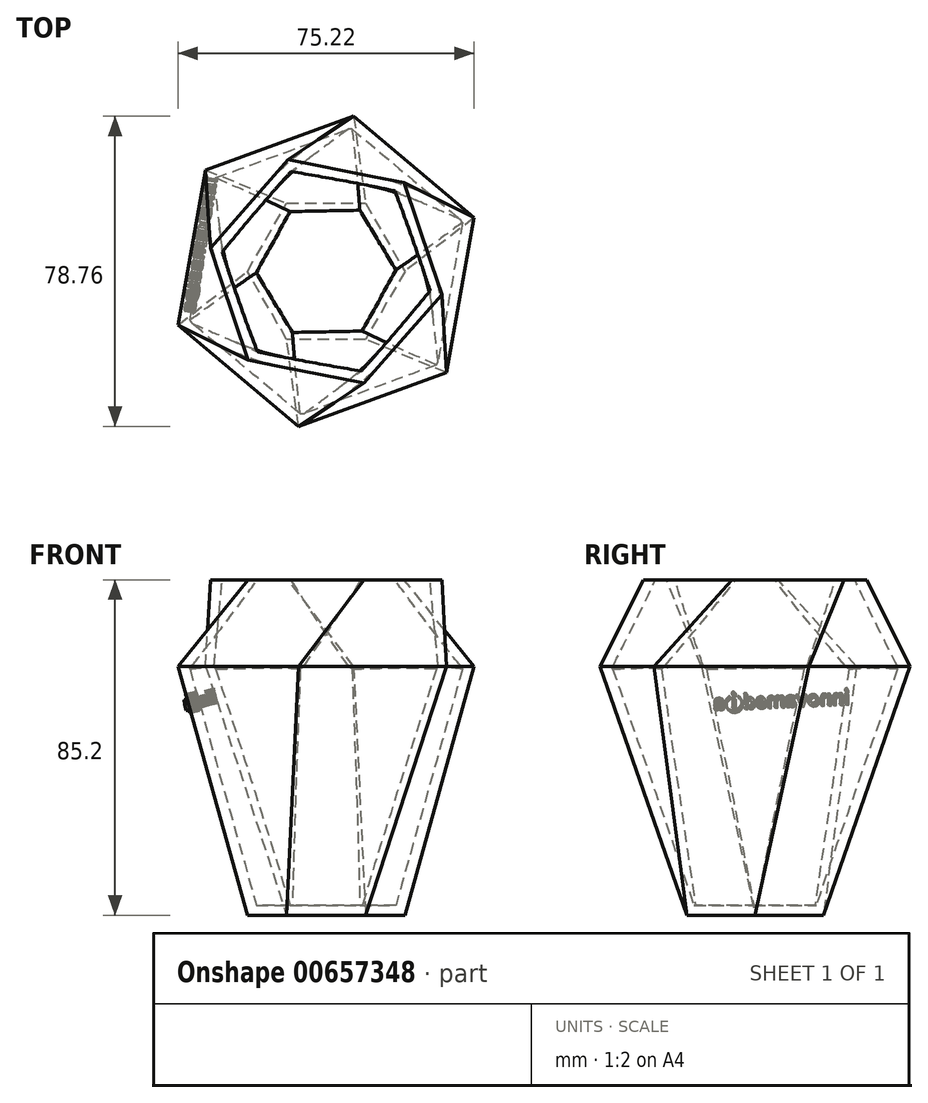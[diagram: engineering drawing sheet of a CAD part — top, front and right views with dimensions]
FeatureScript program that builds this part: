
annotation { "Feature Type Name" : "Feature", "Feature Type Description" : "" }
export const myFeature = defineFeature(function(context is Context, id is Id, definition is map)
    precondition{}
    {
        {
            var Q0;
            Q0=qCreatedBy(makeId("Top.planeOp"),FACE);
            var sketch = newSketch(context, id + "F0", { "sketchPlane" : qUnion([Q0])});
            skCircle(sketch, "E0.cCircle", {"center": v(0, 0) * mm, "radius": 17.32 * mm, "construction": true});
            skLineSegment(sketch, "E0.0", {"start": v(-10, 17.32) * mm, "end": v(10, 17.32) * mm});
            skLineSegment(sketch, "E0.1", {"start": v(10, 17.32) * mm, "end": v(20, 0) * mm});
            skLineSegment(sketch, "E0.2", {"start": v(20, 0) * mm, "end": v(10, -17.32) * mm});
            skLineSegment(sketch, "E0.3", {"start": v(10, -17.32) * mm, "end": v(-10, -17.32) * mm});
            skLineSegment(sketch, "E0.4", {"start": v(-10, -17.32) * mm, "end": v(-20, 0) * mm});
            skLineSegment(sketch, "E0.5", {"start": v(-20, 0) * mm, "end": v(-10, 17.32) * mm});
            skPoint(sketch, "E0.0.midPoint", {"position": v(0, 17.32) * mm});
            skSolve(sketch);
        }
        {
            var Q0;
            Q0=qCreatedBy(makeId("Top.planeOp"),FACE);
            cPlane(context, id + "F1", {"entities" : qUnion([Q0]), "cplaneType" : CPlaneType.OFFSET, "offset" : 63.2 * mm, "width" : 150 * mm, "height" : 150 * mm});
        }
        {
            var Q0;
            Q0=qCreatedBy(id+"F1.planeOp",FACE);
            var sketch = newSketch(context, id + "F2", { "sketchPlane" : qUnion([Q0])});
            skCircle(sketch, "E1.cCircle", {"center": v(0, 0) * mm, "radius": 34.64 * mm, "construction": true});
            skLineSegment(sketch, "E1.0", {"start": v(-30.6, 25.76) * mm, "end": v(7, 39.38) * mm});
            skLineSegment(sketch, "E1.1", {"start": v(7, 39.38) * mm, "end": v(37.6, 13.62) * mm});
            skLineSegment(sketch, "E1.2", {"start": v(37.6, 13.62) * mm, "end": v(30.6, -25.76) * mm});
            skLineSegment(sketch, "E1.3", {"start": v(30.6, -25.76) * mm, "end": v(-7, -39.38) * mm});
            skLineSegment(sketch, "E1.4", {"start": v(-7, -39.38) * mm, "end": v(-37.6, -13.62) * mm});
            skLineSegment(sketch, "E1.5", {"start": v(-37.6, -13.62) * mm, "end": v(-30.6, 25.76) * mm});
            skPoint(sketch, "E1.0.midPoint", {"position": v(-11.8, 32.57) * mm});
            skSolve(sketch);
        }
        {
            var Q0;
            Q0=makeQuery(id+"F2.imprint","IMPRINT",FACE,{"disambiguationData":[TD([[makeQuery(id+"F2.imprint","IMPRINT",EDGE,{"derivedFrom":sQuery(id+"F2.wireOp",EDGE,"E1.0")}),-1.0]])]});
            var Q1;
            Q1=makeQuery(id+"F0.imprint","IMPRINT",FACE,{"disambiguationData":[TD([[makeQuery(id+"F0.imprint","IMPRINT",EDGE,{"derivedFrom":sQuery(id+"F0.wireOp",EDGE,"E0.0")}),-1.0]])]});
            loft(context, id + "F3", {"sheetProfilesArray" : [{ "sheetProfileEntities" : qUnion([Q0]) }, { "sheetProfileEntities" : qUnion([Q1]) }]});
        }
        {
            var Q0;
            Q0=makeQuery(id+"F3.opLoft","CAP_FACE",FACE,{"disambiguationData":[OSD([makeQuery(id+"F2.imprint","IMPRINT",FACE,{"disambiguationData":[TD([[makeQuery(id+"F2.imprint","IMPRINT",EDGE,{"derivedFrom":sQuery(id+"F2.wireOp",EDGE,"E1.0")}),-1.0]])]})])],"isStart":true});
            cPlane(context, id + "F4", {"entities" : qUnion([Q0]), "cplaneType" : CPlaneType.OFFSET, "offset" : 22 * mm, "width" : 150 * mm, "height" : 150 * mm});
        }
        {
            var Q0;
            Q0=qCreatedBy(id+"F4.planeOp",FACE);
            var sketch = newSketch(context, id + "F5", { "sketchPlane" : qUnion([Q0])});
            skCircle(sketch, "E2.cCircle", {"center": v(0, 0) * mm, "radius": 25.98 * mm, "construction": true});
            skLineSegment(sketch, "E2.0", {"start": v(-19.81, -22.53) * mm, "end": v(-29.42, 5.9) * mm});
            skLineSegment(sketch, "E2.1", {"start": v(-29.42, 5.9) * mm, "end": v(-9.6, 28.42) * mm});
            skLineSegment(sketch, "E2.2", {"start": v(-9.6, 28.42) * mm, "end": v(19.81, 22.53) * mm});
            skLineSegment(sketch, "E2.3", {"start": v(19.81, 22.53) * mm, "end": v(29.42, -5.9) * mm});
            skLineSegment(sketch, "E2.4", {"start": v(29.42, -5.9) * mm, "end": v(9.6, -28.42) * mm});
            skLineSegment(sketch, "E2.5", {"start": v(9.6, -28.42) * mm, "end": v(-19.81, -22.53) * mm});
            skSolve(sketch);
        }
        {
            var Q1;
            Q1=makeQuery(id+"F3.opLoft","CAP_FACE",FACE,{"disambiguationData":[OSD([makeQuery(id+"F2.imprint","IMPRINT",FACE,{"disambiguationData":[TD([[makeQuery(id+"F2.imprint","IMPRINT",EDGE,{"derivedFrom":sQuery(id+"F2.wireOp",EDGE,"E1.0")}),-1.0]])]})])],"isStart":true});
            var Q2;
            Q2=makeQuery(id+"F5.imprint","IMPRINT",FACE,{"disambiguationData":[TD([[makeQuery(id+"F5.imprint","IMPRINT",EDGE,{"derivedFrom":sQuery(id+"F5.wireOp",EDGE,"E2.1")}),-1.0]])]});
            loft(context, id + "F6", {"operationType" : NewBodyOperationType.ADD, "sheetProfilesArray" : [{ "sheetProfileEntities" : qUnion([Q1]) }, { "sheetProfileEntities" : qUnion([Q2]) }]});
        }
        {
            var Q0;
            Q0=makeQuery(id+"F6.opLoft","CAP_FACE",FACE,{"disambiguationData":[OSD([makeQuery(id+"F5.imprint","IMPRINT",FACE,{"disambiguationData":[TD([[makeQuery(id+"F5.imprint","IMPRINT",EDGE,{"derivedFrom":sQuery(id+"F5.wireOp",EDGE,"E2.1")}),-1.0]])]})])],"isStart":true});
            shell(context, id + "F7", {"entities" : qUnion([Q0]), "thickness" : 2.5 * mm});
        }
        {
            var Q0;
            Q0=sQuery(id+"F2.wireOp",VERTEX,"E1.0.start");
            var Q1;
            Q1=sQuery(id+"F2.wireOp",VERTEX,"E1.5.start");
            var Q2;
            Q2=sQuery(id+"F0.wireOp",VERTEX,"E0.5.start");
            cPlane(context, id + "F8", {"entities" : qUnion([Q0, Q1, Q2]), "cplaneType" : CPlaneType.THREE_POINT, "offset" : 25 * mm, "width" : 150 * mm, "height" : 150 * mm});
        }
        {
            var Q0;
            Q0=qCreatedBy(id+"F8.planeOp",FACE);
            var sketch = newSketch(context, id + "F9", { "sketchPlane" : qUnion([Q0])});
            skLineSegment(sketch, "E3", {"start": v(-20.7, 62.44) * mm, "end": v(-20.69, 62.48) * mm});
            skLineSegment(sketch, "E4", {"start": v(-20.69, 62.48) * mm, "end": v(-20.63, 62.6) * mm});
            skLineSegment(sketch, "E5", {"start": v(-20.63, 62.6) * mm, "end": v(-20.53, 62.68) * mm});
            skLineSegment(sketch, "E6", {"start": v(-20.53, 62.68) * mm, "end": v(-20.42, 62.73) * mm});
            skLineSegment(sketch, "E7", {"start": v(-20.42, 62.73) * mm, "end": v(-20.28, 62.73) * mm});
            skLineSegment(sketch, "E8", {"start": v(-20.28, 62.73) * mm, "end": v(-20.17, 62.69) * mm});
            skLineSegment(sketch, "E9", {"start": v(-20.17, 62.69) * mm, "end": v(-20.08, 62.61) * mm});
            skLineSegment(sketch, "E10", {"start": v(-20.08, 62.61) * mm, "end": v(-20.02, 62.5) * mm});
            skLineSegment(sketch, "E11", {"start": v(-20.02, 62.5) * mm, "end": v(-20, 62.38) * mm});
            skLineSegment(sketch, "E12", {"start": v(-20, 62.38) * mm, "end": v(-20.02, 62.25) * mm});
            skLineSegment(sketch, "E13", {"start": v(-20.02, 62.25) * mm, "end": v(-20.08, 62.15) * mm});
            skLineSegment(sketch, "E14", {"start": v(-20.08, 62.15) * mm, "end": v(-20.17, 62.08) * mm});
            skLineSegment(sketch, "E15", {"start": v(-20.17, 62.08) * mm, "end": v(-20.29, 62.04) * mm});
            skLineSegment(sketch, "E16", {"start": v(-20.29, 62.04) * mm, "end": v(-20.42, 62.04) * mm});
            skLineSegment(sketch, "E17", {"start": v(-20.42, 62.04) * mm, "end": v(-20.53, 62.07) * mm});
            skLineSegment(sketch, "E18", {"start": v(-20.53, 62.07) * mm, "end": v(-20.62, 62.15) * mm});
            skLineSegment(sketch, "E19", {"start": v(-20.62, 62.15) * mm, "end": v(-20.68, 62.27) * mm});
            skLineSegment(sketch, "E20", {"start": v(-20.68, 62.27) * mm, "end": v(-20.7, 62.3) * mm});
            skLineSegment(sketch, "E21", {"start": v(-20.7, 62.3) * mm, "end": v(-20.7, 62.44) * mm});
            skLineSegment(sketch, "E22", {"start": v(-3.45, 61.2) * mm, "end": v(-3.29, 61.39) * mm});
            skLineSegment(sketch, "E23", {"start": v(-3.29, 61.39) * mm, "end": v(-3.1, 61.52) * mm});
            skLineSegment(sketch, "E24", {"start": v(-3.1, 61.52) * mm, "end": v(-2.89, 61.6) * mm});
            skLineSegment(sketch, "E25", {"start": v(-2.89, 61.6) * mm, "end": v(-2.65, 61.63) * mm});
            skLineSegment(sketch, "E26", {"start": v(-2.65, 61.63) * mm, "end": v(-2.4, 61.6) * mm});
            skLineSegment(sketch, "E27", {"start": v(-2.4, 61.6) * mm, "end": v(-2.2, 61.5) * mm});
            skLineSegment(sketch, "E28", {"start": v(-2.2, 61.5) * mm, "end": v(-2.02, 61.35) * mm});
            skLineSegment(sketch, "E29", {"start": v(-2.02, 61.35) * mm, "end": v(-1.86, 61.17) * mm});
            skLineSegment(sketch, "E30", {"start": v(-1.86, 61.17) * mm, "end": v(-1.7, 61.35) * mm});
            skLineSegment(sketch, "E31", {"start": v(-1.7, 61.35) * mm, "end": v(-1.5, 61.49) * mm});
            skLineSegment(sketch, "E32", {"start": v(-1.5, 61.49) * mm, "end": v(-1.3, 61.58) * mm});
            skLineSegment(sketch, "E33", {"start": v(-1.3, 61.58) * mm, "end": v(-1.06, 61.62) * mm});
            skLineSegment(sketch, "E34", {"start": v(-1.06, 61.62) * mm, "end": v(-0.84, 61.62) * mm});
            skLineSegment(sketch, "E35", {"start": v(-0.84, 61.62) * mm, "end": v(-0.64, 61.57) * mm});
            skLineSegment(sketch, "E36", {"start": v(-0.64, 61.57) * mm, "end": v(-0.45, 61.48) * mm});
            skLineSegment(sketch, "E37", {"start": v(-0.45, 61.48) * mm, "end": v(-0.28, 61.35) * mm});
            skLineSegment(sketch, "E38", {"start": v(-0.28, 61.35) * mm, "end": v(-0.1, 61.1) * mm});
            skLineSegment(sketch, "E39", {"start": v(-0.1, 61.1) * mm, "end": v(-0.04, 60.8) * mm});
            skLineSegment(sketch, "E40", {"start": v(-0.04, 60.8) * mm, "end": v(-0.04, 58.92) * mm});
            skLineSegment(sketch, "E41", {"start": v(-0.04, 58.92) * mm, "end": v(-0.05, 58.87) * mm});
            skLineSegment(sketch, "E42", {"start": v(-0.05, 58.87) * mm, "end": v(-0.1, 58.86) * mm});
            skLineSegment(sketch, "E43", {"start": v(-0.1, 58.86) * mm, "end": v(-0.59, 58.86) * mm});
            skLineSegment(sketch, "E44", {"start": v(-0.59, 58.86) * mm, "end": v(-0.64, 58.87) * mm});
            skLineSegment(sketch, "E45", {"start": v(-0.64, 58.87) * mm, "end": v(-0.65, 58.93) * mm});
            skLineSegment(sketch, "E46", {"start": v(-0.65, 58.93) * mm, "end": v(-0.65, 60.1) * mm});
            skLineSegment(sketch, "E47", {"start": v(-0.65, 60.1) * mm, "end": v(-0.69, 60.63) * mm});
            skLineSegment(sketch, "E48", {"start": v(-0.69, 60.63) * mm, "end": v(-0.76, 60.82) * mm});
            skLineSegment(sketch, "E49", {"start": v(-0.76, 60.82) * mm, "end": v(-0.87, 60.95) * mm});
            skLineSegment(sketch, "E50", {"start": v(-0.87, 60.95) * mm, "end": v(-1.02, 61.02) * mm});
            skLineSegment(sketch, "E51", {"start": v(-1.02, 61.02) * mm, "end": v(-1.23, 61.04) * mm});
            skLineSegment(sketch, "E52", {"start": v(-1.23, 61.04) * mm, "end": v(-1.4, 61) * mm});
            skLineSegment(sketch, "E53", {"start": v(-1.4, 61) * mm, "end": v(-1.56, 60.9) * mm});
            skLineSegment(sketch, "E54", {"start": v(-1.56, 60.9) * mm, "end": v(-1.67, 60.77) * mm});
            skLineSegment(sketch, "E55", {"start": v(-1.67, 60.77) * mm, "end": v(-1.73, 60.6) * mm});
            skLineSegment(sketch, "E56", {"start": v(-1.73, 60.6) * mm, "end": v(-1.75, 60.43) * mm});
            skLineSegment(sketch, "E57", {"start": v(-1.75, 60.43) * mm, "end": v(-1.74, 58.93) * mm});
            skLineSegment(sketch, "E58", {"start": v(-1.74, 58.93) * mm, "end": v(-1.76, 58.87) * mm});
            skLineSegment(sketch, "E59", {"start": v(-1.76, 58.87) * mm, "end": v(-1.82, 58.86) * mm});
            skLineSegment(sketch, "E60", {"start": v(-1.82, 58.86) * mm, "end": v(-2.3, 58.86) * mm});
            skLineSegment(sketch, "E61", {"start": v(-2.3, 58.86) * mm, "end": v(-2.36, 58.87) * mm});
            skLineSegment(sketch, "E62", {"start": v(-2.36, 58.87) * mm, "end": v(-2.38, 58.93) * mm});
            skLineSegment(sketch, "E63", {"start": v(-2.38, 58.93) * mm, "end": v(-2.38, 60.36) * mm});
            skLineSegment(sketch, "E64", {"start": v(-2.38, 60.36) * mm, "end": v(-2.4, 60.56) * mm});
            skLineSegment(sketch, "E65", {"start": v(-2.4, 60.56) * mm, "end": v(-2.45, 60.75) * mm});
            skLineSegment(sketch, "E66", {"start": v(-2.45, 60.75) * mm, "end": v(-2.63, 60.97) * mm});
            skLineSegment(sketch, "E67", {"start": v(-2.63, 60.97) * mm, "end": v(-2.76, 61.03) * mm});
            skLineSegment(sketch, "E68", {"start": v(-2.76, 61.03) * mm, "end": v(-2.9, 61.05) * mm});
            skLineSegment(sketch, "E69", {"start": v(-2.9, 61.05) * mm, "end": v(-3.06, 61.03) * mm});
            skLineSegment(sketch, "E70", {"start": v(-3.06, 61.03) * mm, "end": v(-3.2, 60.96) * mm});
            skLineSegment(sketch, "E71", {"start": v(-3.2, 60.96) * mm, "end": v(-3.4, 60.73) * mm});
            skLineSegment(sketch, "E72", {"start": v(-3.4, 60.73) * mm, "end": v(-3.46, 60.57) * mm});
            skLineSegment(sketch, "E73", {"start": v(-3.46, 60.57) * mm, "end": v(-3.47, 60.4) * mm});
            skLineSegment(sketch, "E74", {"start": v(-3.47, 60.4) * mm, "end": v(-3.47, 58.94) * mm});
            skLineSegment(sketch, "E75", {"start": v(-3.47, 58.94) * mm, "end": v(-3.49, 58.87) * mm});
            skLineSegment(sketch, "E76", {"start": v(-3.49, 58.87) * mm, "end": v(-3.55, 58.86) * mm});
            skLineSegment(sketch, "E77", {"start": v(-3.55, 58.86) * mm, "end": v(-4.04, 58.86) * mm});
            skLineSegment(sketch, "E78", {"start": v(-4.04, 58.86) * mm, "end": v(-4.1, 58.87) * mm});
            skLineSegment(sketch, "E79", {"start": v(-4.1, 58.87) * mm, "end": v(-4.1, 58.92) * mm});
            skLineSegment(sketch, "E80", {"start": v(-4.1, 58.92) * mm, "end": v(-4.1, 61.5) * mm});
            skLineSegment(sketch, "E81", {"start": v(-4.1, 61.5) * mm, "end": v(-4.1, 61.55) * mm});
            skLineSegment(sketch, "E82", {"start": v(-4.1, 61.55) * mm, "end": v(-4.05, 61.57) * mm});
            skLineSegment(sketch, "E83", {"start": v(-4.05, 61.57) * mm, "end": v(-3.53, 61.57) * mm});
            skLineSegment(sketch, "E84", {"start": v(-3.53, 61.57) * mm, "end": v(-3.48, 61.56) * mm});
            skLineSegment(sketch, "E85", {"start": v(-3.48, 61.56) * mm, "end": v(-3.47, 61.5) * mm});
            skLineSegment(sketch, "E86", {"start": v(-3.47, 61.5) * mm, "end": v(-3.47, 61.22) * mm});
            skLineSegment(sketch, "E87", {"start": v(-3.47, 61.22) * mm, "end": v(-3.45, 61.2) * mm});
            skLineSegment(sketch, "E88", {"start": v(5.32, 61.2) * mm, "end": v(5.32, 62.22) * mm});
            skLineSegment(sketch, "E89", {"start": v(5.32, 62.22) * mm, "end": v(5.32, 62.48) * mm});
            skLineSegment(sketch, "E90", {"start": v(5.32, 62.48) * mm, "end": v(5.33, 62.53) * mm});
            skLineSegment(sketch, "E91", {"start": v(5.33, 62.53) * mm, "end": v(5.38, 62.54) * mm});
            skLineSegment(sketch, "E92", {"start": v(5.38, 62.54) * mm, "end": v(5.98, 62.54) * mm});
            skLineSegment(sketch, "E93", {"start": v(5.98, 62.54) * mm, "end": v(6.03, 62.52) * mm});
            skLineSegment(sketch, "E94", {"start": v(6.03, 62.52) * mm, "end": v(6.04, 62.47) * mm});
            skLineSegment(sketch, "E95", {"start": v(6.04, 62.47) * mm, "end": v(6.04, 61.51) * mm});
            skLineSegment(sketch, "E96", {"start": v(6.04, 61.51) * mm, "end": v(6.04, 58.9) * mm});
            skLineSegment(sketch, "E97", {"start": v(6.04, 58.9) * mm, "end": v(6.03, 58.82) * mm});
            skLineSegment(sketch, "E98", {"start": v(6.03, 58.82) * mm, "end": v(5.94, 58.8) * mm});
            skLineSegment(sketch, "E99", {"start": v(5.94, 58.8) * mm, "end": v(5.43, 58.8) * mm});
            skLineSegment(sketch, "E100", {"start": v(5.43, 58.8) * mm, "end": v(5.38, 58.82) * mm});
            skLineSegment(sketch, "E101", {"start": v(5.38, 58.82) * mm, "end": v(5.37, 58.87) * mm});
            skLineSegment(sketch, "E102", {"start": v(5.37, 58.87) * mm, "end": v(5.37, 59.17) * mm});
            skLineSegment(sketch, "E103", {"start": v(5.37, 59.17) * mm, "end": v(5.33, 59.14) * mm});
            skLineSegment(sketch, "E104", {"start": v(5.33, 59.14) * mm, "end": v(5.13, 58.95) * mm});
            skLineSegment(sketch, "E105", {"start": v(5.13, 58.95) * mm, "end": v(4.9, 58.82) * mm});
            skLineSegment(sketch, "E106", {"start": v(4.9, 58.82) * mm, "end": v(4.67, 58.75) * mm});
            skLineSegment(sketch, "E107", {"start": v(4.67, 58.75) * mm, "end": v(4.43, 58.74) * mm});
            skLineSegment(sketch, "E108", {"start": v(4.43, 58.74) * mm, "end": v(4.2, 58.8) * mm});
            skLineSegment(sketch, "E109", {"start": v(4.2, 58.8) * mm, "end": v(3.97, 58.9) * mm});
            skLineSegment(sketch, "E110", {"start": v(3.97, 58.9) * mm, "end": v(3.77, 59.07) * mm});
            skLineSegment(sketch, "E111", {"start": v(3.77, 59.07) * mm, "end": v(3.6, 59.29) * mm});
            skLineSegment(sketch, "E112", {"start": v(3.6, 59.29) * mm, "end": v(3.46, 59.62) * mm});
            skLineSegment(sketch, "E113", {"start": v(3.46, 59.62) * mm, "end": v(3.4, 59.97) * mm});
            skLineSegment(sketch, "E114", {"start": v(3.4, 59.97) * mm, "end": v(3.4, 60.4) * mm});
            skLineSegment(sketch, "E115", {"start": v(3.4, 60.4) * mm, "end": v(3.49, 60.8) * mm});
            skLineSegment(sketch, "E116", {"start": v(3.49, 60.8) * mm, "end": v(3.59, 61.03) * mm});
            skLineSegment(sketch, "E117", {"start": v(3.59, 61.03) * mm, "end": v(3.72, 61.21) * mm});
            skLineSegment(sketch, "E118", {"start": v(3.72, 61.21) * mm, "end": v(3.88, 61.36) * mm});
            skLineSegment(sketch, "E119", {"start": v(3.88, 61.36) * mm, "end": v(4.07, 61.47) * mm});
            skLineSegment(sketch, "E120", {"start": v(4.07, 61.47) * mm, "end": v(4.47, 61.57) * mm});
            skLineSegment(sketch, "E121", {"start": v(4.47, 61.57) * mm, "end": v(4.88, 61.5) * mm});
            skLineSegment(sketch, "E122", {"start": v(4.88, 61.5) * mm, "end": v(5.11, 61.39) * mm});
            skLineSegment(sketch, "E123", {"start": v(5.11, 61.39) * mm, "end": v(5.32, 61.2) * mm});
            skLineSegment(sketch, "E124", {"start": v(5.32, 60.15) * mm, "end": v(5.3, 60.4) * mm});
            skLineSegment(sketch, "E125", {"start": v(5.3, 60.4) * mm, "end": v(5.25, 60.64) * mm});
            skLineSegment(sketch, "E126", {"start": v(5.25, 60.64) * mm, "end": v(5.14, 60.83) * mm});
            skLineSegment(sketch, "E127", {"start": v(5.14, 60.83) * mm, "end": v(4.97, 60.96) * mm});
            skLineSegment(sketch, "E128", {"start": v(4.97, 60.96) * mm, "end": v(4.78, 61.02) * mm});
            skLineSegment(sketch, "E129", {"start": v(4.78, 61.02) * mm, "end": v(4.57, 61) * mm});
            skLineSegment(sketch, "E130", {"start": v(4.57, 61) * mm, "end": v(4.42, 60.93) * mm});
            skLineSegment(sketch, "E131", {"start": v(4.42, 60.93) * mm, "end": v(4.31, 60.83) * mm});
            skLineSegment(sketch, "E132", {"start": v(4.31, 60.83) * mm, "end": v(4.18, 60.56) * mm});
            skLineSegment(sketch, "E133", {"start": v(4.18, 60.56) * mm, "end": v(4.13, 60.14) * mm});
            skLineSegment(sketch, "E134", {"start": v(4.13, 60.14) * mm, "end": v(4.2, 59.73) * mm});
            skLineSegment(sketch, "E135", {"start": v(4.2, 59.73) * mm, "end": v(4.3, 59.52) * mm});
            skLineSegment(sketch, "E136", {"start": v(4.3, 59.52) * mm, "end": v(4.47, 59.37) * mm});
            skLineSegment(sketch, "E137", {"start": v(4.47, 59.37) * mm, "end": v(4.68, 59.3) * mm});
            skLineSegment(sketch, "E138", {"start": v(4.68, 59.3) * mm, "end": v(4.89, 59.33) * mm});
            skLineSegment(sketch, "E139", {"start": v(4.89, 59.33) * mm, "end": v(5.07, 59.44) * mm});
            skLineSegment(sketch, "E140", {"start": v(5.07, 59.44) * mm, "end": v(5.22, 59.62) * mm});
            skLineSegment(sketch, "E141", {"start": v(5.22, 59.62) * mm, "end": v(5.3, 59.88) * mm});
            skLineSegment(sketch, "E142", {"start": v(5.3, 59.88) * mm, "end": v(5.32, 60.15) * mm});
            skLineSegment(sketch, "E143", {"start": v(2.08, 59.95) * mm, "end": v(1.26, 59.95) * mm});
            skLineSegment(sketch, "E144", {"start": v(1.26, 59.95) * mm, "end": v(1.2, 59.93) * mm});
            skLineSegment(sketch, "E145", {"start": v(1.2, 59.93) * mm, "end": v(1.2, 59.88) * mm});
            skLineSegment(sketch, "E146", {"start": v(1.2, 59.88) * mm, "end": v(1.27, 59.6) * mm});
            skLineSegment(sketch, "E147", {"start": v(1.27, 59.6) * mm, "end": v(1.44, 59.4) * mm});
            skLineSegment(sketch, "E148", {"start": v(1.44, 59.4) * mm, "end": v(1.67, 59.29) * mm});
            skLineSegment(sketch, "E149", {"start": v(1.67, 59.29) * mm, "end": v(1.93, 59.3) * mm});
            skLineSegment(sketch, "E150", {"start": v(1.93, 59.3) * mm, "end": v(2.1, 59.42) * mm});
            skLineSegment(sketch, "E151", {"start": v(2.1, 59.42) * mm, "end": v(2.2, 59.6) * mm});
            skLineSegment(sketch, "E152", {"start": v(2.2, 59.6) * mm, "end": v(2.24, 59.65) * mm});
            skLineSegment(sketch, "E153", {"start": v(2.24, 59.65) * mm, "end": v(2.3, 59.66) * mm});
            skLineSegment(sketch, "E154", {"start": v(2.3, 59.66) * mm, "end": v(2.87, 59.56) * mm});
            skLineSegment(sketch, "E155", {"start": v(2.87, 59.56) * mm, "end": v(2.93, 59.54) * mm});
            skLineSegment(sketch, "E156", {"start": v(2.93, 59.54) * mm, "end": v(2.92, 59.47) * mm});
            skLineSegment(sketch, "E157", {"start": v(2.92, 59.47) * mm, "end": v(2.74, 59.17) * mm});
            skLineSegment(sketch, "E158", {"start": v(2.74, 59.17) * mm, "end": v(2.5, 58.94) * mm});
            skLineSegment(sketch, "E159", {"start": v(2.5, 58.94) * mm, "end": v(2.22, 58.8) * mm});
            skLineSegment(sketch, "E160", {"start": v(2.22, 58.8) * mm, "end": v(1.87, 58.74) * mm});
            skLineSegment(sketch, "E161", {"start": v(1.87, 58.74) * mm, "end": v(1.6, 58.74) * mm});
            skLineSegment(sketch, "E162", {"start": v(1.6, 58.74) * mm, "end": v(1.34, 58.79) * mm});
            skLineSegment(sketch, "E163", {"start": v(1.34, 58.79) * mm, "end": v(1.1, 58.88) * mm});
            skLineSegment(sketch, "E164", {"start": v(1.1, 58.88) * mm, "end": v(0.9, 59) * mm});
            skLineSegment(sketch, "E165", {"start": v(0.9, 59) * mm, "end": v(0.74, 59.18) * mm});
            skLineSegment(sketch, "E166", {"start": v(0.74, 59.18) * mm, "end": v(0.6, 59.4) * mm});
            skLineSegment(sketch, "E167", {"start": v(0.6, 59.4) * mm, "end": v(0.49, 59.77) * mm});
            skLineSegment(sketch, "E168", {"start": v(0.49, 59.77) * mm, "end": v(0.45, 60.14) * mm});
            skLineSegment(sketch, "E169", {"start": v(0.45, 60.14) * mm, "end": v(0.49, 60.52) * mm});
            skLineSegment(sketch, "E170", {"start": v(0.49, 60.52) * mm, "end": v(0.61, 60.89) * mm});
            skLineSegment(sketch, "E171", {"start": v(0.61, 60.89) * mm, "end": v(0.82, 61.2) * mm});
            skLineSegment(sketch, "E172", {"start": v(0.82, 61.2) * mm, "end": v(1.12, 61.43) * mm});
            skLineSegment(sketch, "E173", {"start": v(1.12, 61.43) * mm, "end": v(1.48, 61.55) * mm});
            skLineSegment(sketch, "E174", {"start": v(1.48, 61.55) * mm, "end": v(1.87, 61.56) * mm});
            skLineSegment(sketch, "E175", {"start": v(1.87, 61.56) * mm, "end": v(2.15, 61.5) * mm});
            skLineSegment(sketch, "E176", {"start": v(2.15, 61.5) * mm, "end": v(2.4, 61.39) * mm});
            skLineSegment(sketch, "E177", {"start": v(2.4, 61.39) * mm, "end": v(2.6, 61.22) * mm});
            skLineSegment(sketch, "E178", {"start": v(2.6, 61.22) * mm, "end": v(2.77, 61) * mm});
            skLineSegment(sketch, "E179", {"start": v(2.77, 61) * mm, "end": v(2.89, 60.72) * mm});
            skLineSegment(sketch, "E180", {"start": v(2.89, 60.72) * mm, "end": v(2.95, 60.42) * mm});
            skLineSegment(sketch, "E181", {"start": v(2.95, 60.42) * mm, "end": v(2.98, 60.02) * mm});
            skLineSegment(sketch, "E182", {"start": v(2.98, 60.02) * mm, "end": v(2.97, 59.96) * mm});
            skLineSegment(sketch, "E183", {"start": v(2.97, 59.96) * mm, "end": v(2.91, 59.95) * mm});
            skLineSegment(sketch, "E184", {"start": v(2.91, 59.95) * mm, "end": v(2.08, 59.95) * mm});
            skLineSegment(sketch, "E185", {"start": v(1.74, 60.39) * mm, "end": v(2.11, 60.39) * mm});
            skLineSegment(sketch, "E186", {"start": v(2.11, 60.39) * mm, "end": v(2.25, 60.4) * mm});
            skLineSegment(sketch, "E187", {"start": v(2.25, 60.4) * mm, "end": v(2.25, 60.55) * mm});
            skLineSegment(sketch, "E188", {"start": v(2.25, 60.55) * mm, "end": v(2.17, 60.78) * mm});
            skLineSegment(sketch, "E189", {"start": v(2.17, 60.78) * mm, "end": v(2.01, 60.94) * mm});
            skLineSegment(sketch, "E190", {"start": v(2.01, 60.94) * mm, "end": v(1.81, 61.01) * mm});
            skLineSegment(sketch, "E191", {"start": v(1.81, 61.01) * mm, "end": v(1.58, 61) * mm});
            skLineSegment(sketch, "E192", {"start": v(1.58, 61) * mm, "end": v(1.43, 60.92) * mm});
            skLineSegment(sketch, "E193", {"start": v(1.43, 60.92) * mm, "end": v(1.32, 60.8) * mm});
            skLineSegment(sketch, "E194", {"start": v(1.32, 60.8) * mm, "end": v(1.24, 60.64) * mm});
            skLineSegment(sketch, "E195", {"start": v(1.24, 60.64) * mm, "end": v(1.2, 60.45) * mm});
            skLineSegment(sketch, "E196", {"start": v(1.2, 60.45) * mm, "end": v(1.22, 60.4) * mm});
            skLineSegment(sketch, "E197", {"start": v(1.22, 60.4) * mm, "end": v(1.27, 60.39) * mm});
            skLineSegment(sketch, "E198", {"start": v(1.27, 60.39) * mm, "end": v(1.74, 60.39) * mm});
            skLineSegment(sketch, "E199", {"start": v(-5.33, 59.15) * mm, "end": v(-5.5, 59.02) * mm});
            skLineSegment(sketch, "E200", {"start": v(-5.5, 59.02) * mm, "end": v(-5.77, 58.87) * mm});
            skLineSegment(sketch, "E201", {"start": v(-5.77, 58.87) * mm, "end": v(-6.07, 58.8) * mm});
            skLineSegment(sketch, "E202", {"start": v(-6.07, 58.8) * mm, "end": v(-6.36, 58.8) * mm});
            skLineSegment(sketch, "E203", {"start": v(-6.36, 58.8) * mm, "end": v(-6.67, 58.9) * mm});
            skLineSegment(sketch, "E204", {"start": v(-6.67, 58.9) * mm, "end": v(-6.89, 59.05) * mm});
            skLineSegment(sketch, "E205", {"start": v(-6.89, 59.05) * mm, "end": v(-7.04, 59.23) * mm});
            skLineSegment(sketch, "E206", {"start": v(-7.04, 59.23) * mm, "end": v(-7.13, 59.46) * mm});
            skLineSegment(sketch, "E207", {"start": v(-7.13, 59.46) * mm, "end": v(-7.14, 59.72) * mm});
            skLineSegment(sketch, "E208", {"start": v(-7.14, 59.72) * mm, "end": v(-7.1, 59.97) * mm});
            skLineSegment(sketch, "E209", {"start": v(-7.1, 59.97) * mm, "end": v(-6.98, 60.17) * mm});
            skLineSegment(sketch, "E210", {"start": v(-6.98, 60.17) * mm, "end": v(-6.81, 60.33) * mm});
            skLineSegment(sketch, "E211", {"start": v(-6.81, 60.33) * mm, "end": v(-6.58, 60.45) * mm});
            skLineSegment(sketch, "E212", {"start": v(-6.58, 60.45) * mm, "end": v(-6.28, 60.52) * mm});
            skLineSegment(sketch, "E213", {"start": v(-6.28, 60.52) * mm, "end": v(-5.98, 60.54) * mm});
            skLineSegment(sketch, "E214", {"start": v(-5.98, 60.54) * mm, "end": v(-5.68, 60.52) * mm});
            skLineSegment(sketch, "E215", {"start": v(-5.68, 60.52) * mm, "end": v(-5.38, 60.45) * mm});
            skLineSegment(sketch, "E216", {"start": v(-5.38, 60.45) * mm, "end": v(-5.33, 60.43) * mm});
            skLineSegment(sketch, "E217", {"start": v(-5.33, 60.43) * mm, "end": v(-5.32, 60.43) * mm});
            skLineSegment(sketch, "E218", {"start": v(-5.32, 60.43) * mm, "end": v(-5.33, 60.64) * mm});
            skLineSegment(sketch, "E219", {"start": v(-5.33, 60.64) * mm, "end": v(-5.42, 60.82) * mm});
            skLineSegment(sketch, "E220", {"start": v(-5.42, 60.82) * mm, "end": v(-5.58, 60.95) * mm});
            skLineSegment(sketch, "E221", {"start": v(-5.58, 60.95) * mm, "end": v(-5.79, 61.03) * mm});
            skLineSegment(sketch, "E222", {"start": v(-5.79, 61.03) * mm, "end": v(-6.24, 61.03) * mm});
            skLineSegment(sketch, "E223", {"start": v(-6.24, 61.03) * mm, "end": v(-6.67, 60.9) * mm});
            skLineSegment(sketch, "E224", {"start": v(-6.67, 60.9) * mm, "end": v(-6.73, 60.9) * mm});
            skLineSegment(sketch, "E225", {"start": v(-6.73, 60.9) * mm, "end": v(-6.77, 60.94) * mm});
            skLineSegment(sketch, "E226", {"start": v(-6.77, 60.94) * mm, "end": v(-6.9, 61.34) * mm});
            skLineSegment(sketch, "E227", {"start": v(-6.9, 61.34) * mm, "end": v(-6.9, 61.38) * mm});
            skLineSegment(sketch, "E228", {"start": v(-6.9, 61.38) * mm, "end": v(-6.86, 61.4) * mm});
            skLineSegment(sketch, "E229", {"start": v(-6.86, 61.4) * mm, "end": v(-6.44, 61.55) * mm});
            skLineSegment(sketch, "E230", {"start": v(-6.44, 61.55) * mm, "end": v(-6, 61.6) * mm});
            skLineSegment(sketch, "E231", {"start": v(-6, 61.6) * mm, "end": v(-5.66, 61.6) * mm});
            skLineSegment(sketch, "E232", {"start": v(-5.66, 61.6) * mm, "end": v(-5.33, 61.5) * mm});
            skLineSegment(sketch, "E233", {"start": v(-5.33, 61.5) * mm, "end": v(-5.08, 61.37) * mm});
            skLineSegment(sketch, "E234", {"start": v(-5.08, 61.37) * mm, "end": v(-4.9, 61.18) * mm});
            skLineSegment(sketch, "E235", {"start": v(-4.9, 61.18) * mm, "end": v(-4.77, 60.95) * mm});
            skLineSegment(sketch, "E236", {"start": v(-4.77, 60.95) * mm, "end": v(-4.72, 60.67) * mm});
            skLineSegment(sketch, "E237", {"start": v(-4.72, 60.67) * mm, "end": v(-4.7, 59.49) * mm});
            skLineSegment(sketch, "E238", {"start": v(-4.7, 59.49) * mm, "end": v(-4.7, 58.93) * mm});
            skLineSegment(sketch, "E239", {"start": v(-4.7, 58.93) * mm, "end": v(-4.72, 58.88) * mm});
            skLineSegment(sketch, "E240", {"start": v(-4.72, 58.88) * mm, "end": v(-4.77, 58.86) * mm});
            skLineSegment(sketch, "E241", {"start": v(-4.77, 58.86) * mm, "end": v(-5.28, 58.86) * mm});
            skLineSegment(sketch, "E242", {"start": v(-5.28, 58.86) * mm, "end": v(-5.32, 58.88) * mm});
            skLineSegment(sketch, "E243", {"start": v(-5.32, 58.88) * mm, "end": v(-5.34, 58.92) * mm});
            skLineSegment(sketch, "E244", {"start": v(-5.34, 58.92) * mm, "end": v(-5.33, 59.15) * mm});
            skLineSegment(sketch, "E245", {"start": v(-5.98, 59.28) * mm, "end": v(-5.9, 59.28) * mm});
            skLineSegment(sketch, "E246", {"start": v(-5.9, 59.28) * mm, "end": v(-5.65, 59.34) * mm});
            skLineSegment(sketch, "E247", {"start": v(-5.65, 59.34) * mm, "end": v(-5.46, 59.48) * mm});
            skLineSegment(sketch, "E248", {"start": v(-5.46, 59.48) * mm, "end": v(-5.35, 59.67) * mm});
            skLineSegment(sketch, "E249", {"start": v(-5.35, 59.67) * mm, "end": v(-5.31, 59.9) * mm});
            skLineSegment(sketch, "E250", {"start": v(-5.31, 59.9) * mm, "end": v(-5.33, 59.99) * mm});
            skLineSegment(sketch, "E251", {"start": v(-5.33, 59.99) * mm, "end": v(-5.4, 60.03) * mm});
            skLineSegment(sketch, "E252", {"start": v(-5.4, 60.03) * mm, "end": v(-5.92, 60.1) * mm});
            skLineSegment(sketch, "E253", {"start": v(-5.92, 60.1) * mm, "end": v(-6.17, 60.06) * mm});
            skLineSegment(sketch, "E254", {"start": v(-6.17, 60.06) * mm, "end": v(-6.39, 59.95) * mm});
            skLineSegment(sketch, "E255", {"start": v(-6.39, 59.95) * mm, "end": v(-6.49, 59.83) * mm});
            skLineSegment(sketch, "E256", {"start": v(-6.49, 59.83) * mm, "end": v(-6.53, 59.7) * mm});
            skLineSegment(sketch, "E257", {"start": v(-6.53, 59.7) * mm, "end": v(-6.5, 59.55) * mm});
            skLineSegment(sketch, "E258", {"start": v(-6.5, 59.55) * mm, "end": v(-6.4, 59.42) * mm});
            skLineSegment(sketch, "E259", {"start": v(-6.4, 59.42) * mm, "end": v(-6.22, 59.3) * mm});
            skLineSegment(sketch, "E260", {"start": v(-6.22, 59.3) * mm, "end": v(-5.98, 59.28) * mm});
            skLineSegment(sketch, "E261", {"start": v(13.1, 59.14) * mm, "end": v(12.96, 59.04) * mm});
            skLineSegment(sketch, "E262", {"start": v(12.96, 59.04) * mm, "end": v(12.65, 58.87) * mm});
            skLineSegment(sketch, "E263", {"start": v(12.65, 58.87) * mm, "end": v(12.31, 58.8) * mm});
            skLineSegment(sketch, "E264", {"start": v(12.31, 58.8) * mm, "end": v(11.97, 58.83) * mm});
            skLineSegment(sketch, "E265", {"start": v(11.97, 58.83) * mm, "end": v(11.66, 58.96) * mm});
            skLineSegment(sketch, "E266", {"start": v(11.66, 58.96) * mm, "end": v(11.49, 59.1) * mm});
            skLineSegment(sketch, "E267", {"start": v(11.49, 59.1) * mm, "end": v(11.36, 59.27) * mm});
            skLineSegment(sketch, "E268", {"start": v(11.36, 59.27) * mm, "end": v(11.3, 59.47) * mm});
            skLineSegment(sketch, "E269", {"start": v(11.3, 59.47) * mm, "end": v(11.28, 59.7) * mm});
            skLineSegment(sketch, "E270", {"start": v(11.28, 59.7) * mm, "end": v(11.32, 59.94) * mm});
            skLineSegment(sketch, "E271", {"start": v(11.32, 59.94) * mm, "end": v(11.42, 60.14) * mm});
            skLineSegment(sketch, "E272", {"start": v(11.42, 60.14) * mm, "end": v(11.58, 60.3) * mm});
            skLineSegment(sketch, "E273", {"start": v(11.58, 60.3) * mm, "end": v(11.8, 60.43) * mm});
            skLineSegment(sketch, "E274", {"start": v(11.8, 60.43) * mm, "end": v(12.15, 60.53) * mm});
            skLineSegment(sketch, "E275", {"start": v(12.15, 60.53) * mm, "end": v(12.53, 60.54) * mm});
            skLineSegment(sketch, "E276", {"start": v(12.53, 60.54) * mm, "end": v(12.82, 60.51) * mm});
            skLineSegment(sketch, "E277", {"start": v(12.82, 60.51) * mm, "end": v(13.1, 60.43) * mm});
            skLineSegment(sketch, "E278", {"start": v(13.1, 60.43) * mm, "end": v(13.1, 60.6) * mm});
            skLineSegment(sketch, "E279", {"start": v(13.1, 60.6) * mm, "end": v(13.04, 60.76) * mm});
            skLineSegment(sketch, "E280", {"start": v(13.04, 60.76) * mm, "end": v(12.93, 60.9) * mm});
            skLineSegment(sketch, "E281", {"start": v(12.93, 60.9) * mm, "end": v(12.77, 60.98) * mm});
            skLineSegment(sketch, "E282", {"start": v(12.77, 60.98) * mm, "end": v(12.44, 61.04) * mm});
            skLineSegment(sketch, "E283", {"start": v(12.44, 61.04) * mm, "end": v(12.1, 61) * mm});
            skLineSegment(sketch, "E284", {"start": v(12.1, 61) * mm, "end": v(11.75, 60.9) * mm});
            skLineSegment(sketch, "E285", {"start": v(11.75, 60.9) * mm, "end": v(11.7, 60.89) * mm});
            skLineSegment(sketch, "E286", {"start": v(11.7, 60.89) * mm, "end": v(11.66, 60.94) * mm});
            skLineSegment(sketch, "E287", {"start": v(11.66, 60.94) * mm, "end": v(11.53, 61.34) * mm});
            skLineSegment(sketch, "E288", {"start": v(11.53, 61.34) * mm, "end": v(11.53, 61.38) * mm});
            skLineSegment(sketch, "E289", {"start": v(11.53, 61.38) * mm, "end": v(11.57, 61.4) * mm});
            skLineSegment(sketch, "E290", {"start": v(11.57, 61.4) * mm, "end": v(11.89, 61.52) * mm});
            skLineSegment(sketch, "E291", {"start": v(11.89, 61.52) * mm, "end": v(12.22, 61.6) * mm});
            skLineSegment(sketch, "E292", {"start": v(12.22, 61.6) * mm, "end": v(12.62, 61.61) * mm});
            skLineSegment(sketch, "E293", {"start": v(12.62, 61.61) * mm, "end": v(13.02, 61.54) * mm});
            skLineSegment(sketch, "E294", {"start": v(13.02, 61.54) * mm, "end": v(13.31, 61.4) * mm});
            skLineSegment(sketch, "E295", {"start": v(13.31, 61.4) * mm, "end": v(13.53, 61.2) * mm});
            skLineSegment(sketch, "E296", {"start": v(13.53, 61.2) * mm, "end": v(13.67, 60.92) * mm});
            skLineSegment(sketch, "E297", {"start": v(13.67, 60.92) * mm, "end": v(13.72, 60.6) * mm});
            skLineSegment(sketch, "E298", {"start": v(13.72, 60.6) * mm, "end": v(13.72, 58.92) * mm});
            skLineSegment(sketch, "E299", {"start": v(13.72, 58.92) * mm, "end": v(13.71, 58.87) * mm});
            skLineSegment(sketch, "E300", {"start": v(13.71, 58.87) * mm, "end": v(13.66, 58.86) * mm});
            skLineSegment(sketch, "E301", {"start": v(13.66, 58.86) * mm, "end": v(13.15, 58.86) * mm});
            skLineSegment(sketch, "E302", {"start": v(13.15, 58.86) * mm, "end": v(13.1, 58.87) * mm});
            skLineSegment(sketch, "E303", {"start": v(13.1, 58.87) * mm, "end": v(13.1, 58.93) * mm});
            skLineSegment(sketch, "E304", {"start": v(13.1, 58.93) * mm, "end": v(13.1, 59.14) * mm});
            skLineSegment(sketch, "E305", {"start": v(12.43, 59.28) * mm, "end": v(12.62, 59.3) * mm});
            skLineSegment(sketch, "E306", {"start": v(12.62, 59.3) * mm, "end": v(12.83, 59.38) * mm});
            skLineSegment(sketch, "E307", {"start": v(12.83, 59.38) * mm, "end": v(13, 59.5) * mm});
            skLineSegment(sketch, "E308", {"start": v(13, 59.5) * mm, "end": v(13.09, 59.68) * mm});
            skLineSegment(sketch, "E309", {"start": v(13.09, 59.68) * mm, "end": v(13.11, 59.9) * mm});
            skLineSegment(sketch, "E310", {"start": v(13.11, 59.9) * mm, "end": v(13.09, 59.98) * mm});
            skLineSegment(sketch, "E311", {"start": v(13.09, 59.98) * mm, "end": v(13.01, 60.03) * mm});
            skLineSegment(sketch, "E312", {"start": v(13.01, 60.03) * mm, "end": v(12.58, 60.09) * mm});
            skLineSegment(sketch, "E313", {"start": v(12.58, 60.09) * mm, "end": v(12.31, 60.07) * mm});
            skLineSegment(sketch, "E314", {"start": v(12.31, 60.07) * mm, "end": v(12.07, 59.97) * mm});
            skLineSegment(sketch, "E315", {"start": v(12.07, 59.97) * mm, "end": v(11.95, 59.84) * mm});
            skLineSegment(sketch, "E316", {"start": v(11.95, 59.84) * mm, "end": v(11.9, 59.68) * mm});
            skLineSegment(sketch, "E317", {"start": v(11.9, 59.68) * mm, "end": v(11.94, 59.52) * mm});
            skLineSegment(sketch, "E318", {"start": v(11.94, 59.52) * mm, "end": v(12.06, 59.39) * mm});
            skLineSegment(sketch, "E319", {"start": v(12.06, 59.39) * mm, "end": v(12.24, 59.3) * mm});
            skLineSegment(sketch, "E320", {"start": v(12.24, 59.3) * mm, "end": v(12.43, 59.28) * mm});
            skLineSegment(sketch, "E321", {"start": v(-13.15, 60.22) * mm, "end": v(-13.12, 60.5) * mm});
            skLineSegment(sketch, "E322", {"start": v(-13.12, 60.5) * mm, "end": v(-13.04, 60.76) * mm});
            skLineSegment(sketch, "E323", {"start": v(-13.04, 60.76) * mm, "end": v(-12.91, 61) * mm});
            skLineSegment(sketch, "E324", {"start": v(-12.91, 61) * mm, "end": v(-12.74, 61.2) * mm});
            skLineSegment(sketch, "E325", {"start": v(-12.74, 61.2) * mm, "end": v(-12.53, 61.38) * mm});
            skLineSegment(sketch, "E326", {"start": v(-12.53, 61.38) * mm, "end": v(-12.29, 61.5) * mm});
            skLineSegment(sketch, "E327", {"start": v(-12.29, 61.5) * mm, "end": v(-12.02, 61.6) * mm});
            skLineSegment(sketch, "E328", {"start": v(-12.02, 61.6) * mm, "end": v(-11.73, 61.62) * mm});
            skLineSegment(sketch, "E329", {"start": v(-11.73, 61.62) * mm, "end": v(-11.44, 61.6) * mm});
            skLineSegment(sketch, "E330", {"start": v(-11.44, 61.6) * mm, "end": v(-11.17, 61.52) * mm});
            skLineSegment(sketch, "E331", {"start": v(-11.17, 61.52) * mm, "end": v(-10.92, 61.4) * mm});
            skLineSegment(sketch, "E332", {"start": v(-10.92, 61.4) * mm, "end": v(-10.71, 61.23) * mm});
            skLineSegment(sketch, "E333", {"start": v(-10.71, 61.23) * mm, "end": v(-10.54, 61.02) * mm});
            skLineSegment(sketch, "E334", {"start": v(-10.54, 61.02) * mm, "end": v(-10.4, 60.78) * mm});
            skLineSegment(sketch, "E335", {"start": v(-10.4, 60.78) * mm, "end": v(-10.32, 60.51) * mm});
            skLineSegment(sketch, "E336", {"start": v(-10.32, 60.51) * mm, "end": v(-10.3, 60.22) * mm});
            skLineSegment(sketch, "E337", {"start": v(-10.3, 60.22) * mm, "end": v(-10.32, 59.94) * mm});
            skLineSegment(sketch, "E338", {"start": v(-10.32, 59.94) * mm, "end": v(-10.4, 59.67) * mm});
            skLineSegment(sketch, "E339", {"start": v(-10.4, 59.67) * mm, "end": v(-10.53, 59.43) * mm});
            skLineSegment(sketch, "E340", {"start": v(-10.53, 59.43) * mm, "end": v(-10.7, 59.22) * mm});
            skLineSegment(sketch, "E341", {"start": v(-10.7, 59.22) * mm, "end": v(-10.9, 59.04) * mm});
            skLineSegment(sketch, "E342", {"start": v(-10.9, 59.04) * mm, "end": v(-11.14, 58.91) * mm});
            skLineSegment(sketch, "E343", {"start": v(-11.14, 58.91) * mm, "end": v(-11.4, 58.83) * mm});
            skLineSegment(sketch, "E344", {"start": v(-11.4, 58.83) * mm, "end": v(-11.7, 58.8) * mm});
            skLineSegment(sketch, "E345", {"start": v(-11.7, 58.8) * mm, "end": v(-12, 58.83) * mm});
            skLineSegment(sketch, "E346", {"start": v(-12, 58.83) * mm, "end": v(-12.27, 58.9) * mm});
            skLineSegment(sketch, "E347", {"start": v(-12.27, 58.9) * mm, "end": v(-12.52, 59.03) * mm});
            skLineSegment(sketch, "E348", {"start": v(-12.52, 59.03) * mm, "end": v(-12.73, 59.2) * mm});
            skLineSegment(sketch, "E349", {"start": v(-12.73, 59.2) * mm, "end": v(-12.9, 59.4) * mm});
            skLineSegment(sketch, "E350", {"start": v(-12.9, 59.4) * mm, "end": v(-13.04, 59.64) * mm});
            skLineSegment(sketch, "E351", {"start": v(-13.04, 59.64) * mm, "end": v(-13.12, 59.92) * mm});
            skLineSegment(sketch, "E352", {"start": v(-13.12, 59.92) * mm, "end": v(-13.15, 60.22) * mm});
            skLineSegment(sketch, "E353", {"start": v(-12.52, 60.22) * mm, "end": v(-12.5, 59.96) * mm});
            skLineSegment(sketch, "E354", {"start": v(-12.5, 59.96) * mm, "end": v(-12.4, 59.74) * mm});
            skLineSegment(sketch, "E355", {"start": v(-12.4, 59.74) * mm, "end": v(-12.27, 59.57) * mm});
            skLineSegment(sketch, "E356", {"start": v(-12.27, 59.57) * mm, "end": v(-12.11, 59.45) * mm});
            skLineSegment(sketch, "E357", {"start": v(-12.11, 59.45) * mm, "end": v(-11.93, 59.37) * mm});
            skLineSegment(sketch, "E358", {"start": v(-11.93, 59.37) * mm, "end": v(-11.74, 59.34) * mm});
            skLineSegment(sketch, "E359", {"start": v(-11.74, 59.34) * mm, "end": v(-11.55, 59.35) * mm});
            skLineSegment(sketch, "E360", {"start": v(-11.55, 59.35) * mm, "end": v(-11.37, 59.4) * mm});
            skLineSegment(sketch, "E361", {"start": v(-11.37, 59.4) * mm, "end": v(-11.21, 59.51) * mm});
            skLineSegment(sketch, "E362", {"start": v(-11.21, 59.51) * mm, "end": v(-11.08, 59.67) * mm});
            skLineSegment(sketch, "E363", {"start": v(-11.08, 59.67) * mm, "end": v(-10.96, 59.91) * mm});
            skLineSegment(sketch, "E364", {"start": v(-10.96, 59.91) * mm, "end": v(-10.91, 60.17) * mm});
            skLineSegment(sketch, "E365", {"start": v(-10.91, 60.17) * mm, "end": v(-10.94, 60.43) * mm});
            skLineSegment(sketch, "E366", {"start": v(-10.94, 60.43) * mm, "end": v(-11.05, 60.68) * mm});
            skLineSegment(sketch, "E367", {"start": v(-11.05, 60.68) * mm, "end": v(-11.2, 60.88) * mm});
            skLineSegment(sketch, "E368", {"start": v(-11.2, 60.88) * mm, "end": v(-11.39, 61) * mm});
            skLineSegment(sketch, "E369", {"start": v(-11.39, 61) * mm, "end": v(-11.6, 61.06) * mm});
            skLineSegment(sketch, "E370", {"start": v(-11.6, 61.06) * mm, "end": v(-11.85, 61.06) * mm});
            skLineSegment(sketch, "E371", {"start": v(-11.85, 61.06) * mm, "end": v(-12.06, 61) * mm});
            skLineSegment(sketch, "E372", {"start": v(-12.06, 61) * mm, "end": v(-12.24, 60.9) * mm});
            skLineSegment(sketch, "E373", {"start": v(-12.24, 60.9) * mm, "end": v(-12.37, 60.75) * mm});
            skLineSegment(sketch, "E374", {"start": v(-12.37, 60.75) * mm, "end": v(-12.47, 60.55) * mm});
            skLineSegment(sketch, "E375", {"start": v(-12.47, 60.55) * mm, "end": v(-12.52, 60.22) * mm});
            skLineSegment(sketch, "E376", {"start": v(-18.64, 61.18) * mm, "end": v(-18.57, 61.26) * mm});
            skLineSegment(sketch, "E377", {"start": v(-18.57, 61.26) * mm, "end": v(-18.45, 61.4) * mm});
            skLineSegment(sketch, "E378", {"start": v(-18.45, 61.4) * mm, "end": v(-18.3, 61.5) * mm});
            skLineSegment(sketch, "E379", {"start": v(-18.3, 61.5) * mm, "end": v(-17.94, 61.61) * mm});
            skLineSegment(sketch, "E380", {"start": v(-17.94, 61.61) * mm, "end": v(-17.56, 61.59) * mm});
            skLineSegment(sketch, "E381", {"start": v(-17.56, 61.59) * mm, "end": v(-17.38, 61.53) * mm});
            skLineSegment(sketch, "E382", {"start": v(-17.38, 61.53) * mm, "end": v(-17.22, 61.43) * mm});
            skLineSegment(sketch, "E383", {"start": v(-17.22, 61.43) * mm, "end": v(-17.07, 61.27) * mm});
            skLineSegment(sketch, "E384", {"start": v(-17.07, 61.27) * mm, "end": v(-16.96, 61.1) * mm});
            skLineSegment(sketch, "E385", {"start": v(-16.96, 61.1) * mm, "end": v(-16.9, 60.9) * mm});
            skLineSegment(sketch, "E386", {"start": v(-16.9, 60.9) * mm, "end": v(-16.87, 60.68) * mm});
            skLineSegment(sketch, "E387", {"start": v(-16.87, 60.68) * mm, "end": v(-16.87, 58.92) * mm});
            skLineSegment(sketch, "E388", {"start": v(-16.87, 58.92) * mm, "end": v(-16.89, 58.87) * mm});
            skLineSegment(sketch, "E389", {"start": v(-16.89, 58.87) * mm, "end": v(-16.93, 58.86) * mm});
            skLineSegment(sketch, "E390", {"start": v(-16.93, 58.86) * mm, "end": v(-17.43, 58.86) * mm});
            skLineSegment(sketch, "E391", {"start": v(-17.43, 58.86) * mm, "end": v(-17.49, 58.88) * mm});
            skLineSegment(sketch, "E392", {"start": v(-17.49, 58.88) * mm, "end": v(-17.5, 58.94) * mm});
            skLineSegment(sketch, "E393", {"start": v(-17.5, 58.94) * mm, "end": v(-17.5, 60.44) * mm});
            skLineSegment(sketch, "E394", {"start": v(-17.5, 60.44) * mm, "end": v(-17.51, 60.62) * mm});
            skLineSegment(sketch, "E395", {"start": v(-17.51, 60.62) * mm, "end": v(-17.59, 60.81) * mm});
            skLineSegment(sketch, "E396", {"start": v(-17.59, 60.81) * mm, "end": v(-17.72, 60.95) * mm});
            skLineSegment(sketch, "E397", {"start": v(-17.72, 60.95) * mm, "end": v(-17.9, 61.03) * mm});
            skLineSegment(sketch, "E398", {"start": v(-17.9, 61.03) * mm, "end": v(-18.12, 61.04) * mm});
            skLineSegment(sketch, "E399", {"start": v(-18.12, 61.04) * mm, "end": v(-18.32, 60.99) * mm});
            skLineSegment(sketch, "E400", {"start": v(-18.32, 60.99) * mm, "end": v(-18.49, 60.87) * mm});
            skLineSegment(sketch, "E401", {"start": v(-18.49, 60.87) * mm, "end": v(-18.6, 60.7) * mm});
            skLineSegment(sketch, "E402", {"start": v(-18.6, 60.7) * mm, "end": v(-18.64, 60.5) * mm});
            skLineSegment(sketch, "E403", {"start": v(-18.64, 60.5) * mm, "end": v(-18.64, 58.96) * mm});
            skLineSegment(sketch, "E404", {"start": v(-18.64, 58.96) * mm, "end": v(-18.65, 58.87) * mm});
            skLineSegment(sketch, "E405", {"start": v(-18.65, 58.87) * mm, "end": v(-18.74, 58.86) * mm});
            skLineSegment(sketch, "E406", {"start": v(-18.74, 58.86) * mm, "end": v(-19.21, 58.86) * mm});
            skLineSegment(sketch, "E407", {"start": v(-19.21, 58.86) * mm, "end": v(-19.26, 58.87) * mm});
            skLineSegment(sketch, "E408", {"start": v(-19.26, 58.87) * mm, "end": v(-19.27, 58.92) * mm});
            skLineSegment(sketch, "E409", {"start": v(-19.27, 58.92) * mm, "end": v(-19.27, 61.5) * mm});
            skLineSegment(sketch, "E410", {"start": v(-19.27, 61.5) * mm, "end": v(-19.26, 61.55) * mm});
            skLineSegment(sketch, "E411", {"start": v(-19.26, 61.55) * mm, "end": v(-19.21, 61.57) * mm});
            skLineSegment(sketch, "E412", {"start": v(-19.21, 61.57) * mm, "end": v(-18.7, 61.57) * mm});
            skLineSegment(sketch, "E413", {"start": v(-18.7, 61.57) * mm, "end": v(-18.65, 61.55) * mm});
            skLineSegment(sketch, "E414", {"start": v(-18.65, 61.55) * mm, "end": v(-18.64, 61.5) * mm});
            skLineSegment(sketch, "E415", {"start": v(-18.64, 61.5) * mm, "end": v(-18.64, 61.18) * mm});
            skLineSegment(sketch, "E416", {"start": v(-15.5, 61.18) * mm, "end": v(-15.34, 61.36) * mm});
            skLineSegment(sketch, "E417", {"start": v(-15.34, 61.36) * mm, "end": v(-15.02, 61.56) * mm});
            skLineSegment(sketch, "E418", {"start": v(-15.02, 61.56) * mm, "end": v(-14.66, 61.62) * mm});
            skLineSegment(sketch, "E419", {"start": v(-14.66, 61.62) * mm, "end": v(-14.3, 61.55) * mm});
            skLineSegment(sketch, "E420", {"start": v(-14.3, 61.55) * mm, "end": v(-14, 61.35) * mm});
            skLineSegment(sketch, "E421", {"start": v(-14, 61.35) * mm, "end": v(-13.81, 61.08) * mm});
            skLineSegment(sketch, "E422", {"start": v(-13.81, 61.08) * mm, "end": v(-13.74, 60.76) * mm});
            skLineSegment(sketch, "E423", {"start": v(-13.74, 60.76) * mm, "end": v(-13.73, 60.07) * mm});
            skLineSegment(sketch, "E424", {"start": v(-13.73, 60.07) * mm, "end": v(-13.73, 58.94) * mm});
            skLineSegment(sketch, "E425", {"start": v(-13.73, 58.94) * mm, "end": v(-13.75, 58.88) * mm});
            skLineSegment(sketch, "E426", {"start": v(-13.75, 58.88) * mm, "end": v(-13.8, 58.86) * mm});
            skLineSegment(sketch, "E427", {"start": v(-13.8, 58.86) * mm, "end": v(-14.3, 58.86) * mm});
            skLineSegment(sketch, "E428", {"start": v(-14.3, 58.86) * mm, "end": v(-14.35, 58.88) * mm});
            skLineSegment(sketch, "E429", {"start": v(-14.35, 58.88) * mm, "end": v(-14.36, 58.93) * mm});
            skLineSegment(sketch, "E430", {"start": v(-14.36, 58.93) * mm, "end": v(-14.36, 60.45) * mm});
            skLineSegment(sketch, "E431", {"start": v(-14.36, 60.45) * mm, "end": v(-14.38, 60.68) * mm});
            skLineSegment(sketch, "E432", {"start": v(-14.38, 60.68) * mm, "end": v(-14.5, 60.88) * mm});
            skLineSegment(sketch, "E433", {"start": v(-14.5, 60.88) * mm, "end": v(-14.69, 61) * mm});
            skLineSegment(sketch, "E434", {"start": v(-14.69, 61) * mm, "end": v(-14.92, 61.05) * mm});
            skLineSegment(sketch, "E435", {"start": v(-14.92, 61.05) * mm, "end": v(-15.17, 61) * mm});
            skLineSegment(sketch, "E436", {"start": v(-15.17, 61) * mm, "end": v(-15.31, 60.9) * mm});
            skLineSegment(sketch, "E437", {"start": v(-15.31, 60.9) * mm, "end": v(-15.42, 60.78) * mm});
            skLineSegment(sketch, "E438", {"start": v(-15.42, 60.78) * mm, "end": v(-15.48, 60.63) * mm});
            skLineSegment(sketch, "E439", {"start": v(-15.48, 60.63) * mm, "end": v(-15.5, 60.46) * mm});
            skLineSegment(sketch, "E440", {"start": v(-15.5, 60.46) * mm, "end": v(-15.5, 58.94) * mm});
            skLineSegment(sketch, "E441", {"start": v(-15.5, 58.94) * mm, "end": v(-15.52, 58.88) * mm});
            skLineSegment(sketch, "E442", {"start": v(-15.52, 58.88) * mm, "end": v(-15.58, 58.86) * mm});
            skLineSegment(sketch, "E443", {"start": v(-15.58, 58.86) * mm, "end": v(-16.07, 58.86) * mm});
            skLineSegment(sketch, "E444", {"start": v(-16.07, 58.86) * mm, "end": v(-16.12, 58.88) * mm});
            skLineSegment(sketch, "E445", {"start": v(-16.12, 58.88) * mm, "end": v(-16.13, 58.93) * mm});
            skLineSegment(sketch, "E446", {"start": v(-16.13, 58.93) * mm, "end": v(-16.13, 61.5) * mm});
            skLineSegment(sketch, "E447", {"start": v(-16.13, 61.5) * mm, "end": v(-16.12, 61.55) * mm});
            skLineSegment(sketch, "E448", {"start": v(-16.12, 61.55) * mm, "end": v(-16.07, 61.57) * mm});
            skLineSegment(sketch, "E449", {"start": v(-16.07, 61.57) * mm, "end": v(-15.56, 61.57) * mm});
            skLineSegment(sketch, "E450", {"start": v(-15.56, 61.57) * mm, "end": v(-15.51, 61.55) * mm});
            skLineSegment(sketch, "E451", {"start": v(-15.51, 61.55) * mm, "end": v(-15.5, 61.5) * mm});
            skLineSegment(sketch, "E452", {"start": v(-15.5, 61.5) * mm, "end": v(-15.5, 61.18) * mm});
            skLineSegment(sketch, "E453", {"start": v(-10.08, 61.57) * mm, "end": v(-9.45, 61.57) * mm});
            skLineSegment(sketch, "E454", {"start": v(-9.45, 61.57) * mm, "end": v(-9.4, 61.54) * mm});
            skLineSegment(sketch, "E455", {"start": v(-9.4, 61.54) * mm, "end": v(-9.4, 61.5) * mm});
            skLineSegment(sketch, "E456", {"start": v(-9.4, 61.5) * mm, "end": v(-8.9, 60.14) * mm});
            skLineSegment(sketch, "E457", {"start": v(-8.9, 60.14) * mm, "end": v(-8.75, 59.69) * mm});
            skLineSegment(sketch, "E458", {"start": v(-8.75, 59.69) * mm, "end": v(-8.72, 59.64) * mm});
            skLineSegment(sketch, "E459", {"start": v(-8.72, 59.64) * mm, "end": v(-8.67, 59.69) * mm});
            skLineSegment(sketch, "E460", {"start": v(-8.67, 59.69) * mm, "end": v(-8.6, 59.88) * mm});
            skLineSegment(sketch, "E461", {"start": v(-8.6, 59.88) * mm, "end": v(-8.02, 61.5) * mm});
            skLineSegment(sketch, "E462", {"start": v(-8.02, 61.5) * mm, "end": v(-7.98, 61.55) * mm});
            skLineSegment(sketch, "E463", {"start": v(-7.98, 61.55) * mm, "end": v(-7.92, 61.57) * mm});
            skLineSegment(sketch, "E464", {"start": v(-7.92, 61.57) * mm, "end": v(-7.4, 61.57) * mm});
            skLineSegment(sketch, "E465", {"start": v(-7.4, 61.57) * mm, "end": v(-7.35, 61.55) * mm});
            skLineSegment(sketch, "E466", {"start": v(-7.35, 61.55) * mm, "end": v(-7.36, 61.5) * mm});
            skLineSegment(sketch, "E467", {"start": v(-7.36, 61.5) * mm, "end": v(-7.66, 60.76) * mm});
            skLineSegment(sketch, "E468", {"start": v(-7.66, 60.76) * mm, "end": v(-8.4, 58.9) * mm});
            skLineSegment(sketch, "E469", {"start": v(-8.4, 58.9) * mm, "end": v(-8.43, 58.86) * mm});
            skLineSegment(sketch, "E470", {"start": v(-8.43, 58.86) * mm, "end": v(-8.49, 58.84) * mm});
            skLineSegment(sketch, "E471", {"start": v(-8.49, 58.84) * mm, "end": v(-8.95, 58.85) * mm});
            skLineSegment(sketch, "E472", {"start": v(-8.95, 58.85) * mm, "end": v(-9.01, 58.87) * mm});
            skLineSegment(sketch, "E473", {"start": v(-9.01, 58.87) * mm, "end": v(-9.47, 60.03) * mm});
            skLineSegment(sketch, "E474", {"start": v(-9.47, 60.03) * mm, "end": v(-10.03, 61.42) * mm});
            skLineSegment(sketch, "E475", {"start": v(-10.03, 61.42) * mm, "end": v(-10.08, 61.57) * mm});
            skLineSegment(sketch, "E476", {"start": v(8.71, 57.95) * mm, "end": v(8.32, 57.98) * mm});
            skLineSegment(sketch, "E477", {"start": v(8.32, 57.98) * mm, "end": v(7.94, 58.09) * mm});
            skLineSegment(sketch, "E478", {"start": v(7.94, 58.09) * mm, "end": v(7.6, 58.25) * mm});
            skLineSegment(sketch, "E479", {"start": v(7.6, 58.25) * mm, "end": v(7.28, 58.47) * mm});
            skLineSegment(sketch, "E480", {"start": v(7.28, 58.47) * mm, "end": v(7.01, 58.75) * mm});
            skLineSegment(sketch, "E481", {"start": v(7.01, 58.75) * mm, "end": v(6.8, 59.06) * mm});
            skLineSegment(sketch, "E482", {"start": v(6.8, 59.06) * mm, "end": v(6.64, 59.41) * mm});
            skLineSegment(sketch, "E483", {"start": v(6.64, 59.41) * mm, "end": v(6.55, 59.8) * mm});
            skLineSegment(sketch, "E484", {"start": v(6.55, 59.8) * mm, "end": v(6.53, 60.39) * mm});
            skLineSegment(sketch, "E485", {"start": v(6.53, 60.39) * mm, "end": v(6.67, 60.93) * mm});
            skLineSegment(sketch, "E486", {"start": v(6.67, 60.93) * mm, "end": v(6.94, 61.41) * mm});
            skLineSegment(sketch, "E487", {"start": v(6.94, 61.41) * mm, "end": v(7.35, 61.84) * mm});
            skLineSegment(sketch, "E488", {"start": v(7.35, 61.84) * mm, "end": v(7.42, 61.89) * mm});
            skLineSegment(sketch, "E489", {"start": v(7.42, 61.89) * mm, "end": v(7.5, 61.89) * mm});
            skLineSegment(sketch, "E490", {"start": v(7.5, 61.89) * mm, "end": v(7.6, 61.79) * mm});
            skLineSegment(sketch, "E491", {"start": v(7.6, 61.79) * mm, "end": v(7.58, 61.71) * mm});
            skLineSegment(sketch, "E492", {"start": v(7.58, 61.71) * mm, "end": v(7.53, 61.66) * mm});
            skLineSegment(sketch, "E493", {"start": v(7.53, 61.66) * mm, "end": v(7.2, 61.32) * mm});
            skLineSegment(sketch, "E494", {"start": v(7.2, 61.32) * mm, "end": v(6.93, 60.88) * mm});
            skLineSegment(sketch, "E495", {"start": v(6.93, 60.88) * mm, "end": v(6.8, 60.4) * mm});
            skLineSegment(sketch, "E496", {"start": v(6.8, 60.4) * mm, "end": v(6.8, 59.93) * mm});
            skLineSegment(sketch, "E497", {"start": v(6.8, 59.93) * mm, "end": v(6.9, 59.47) * mm});
            skLineSegment(sketch, "E498", {"start": v(6.9, 59.47) * mm, "end": v(7.12, 59.05) * mm});
            skLineSegment(sketch, "E499", {"start": v(7.12, 59.05) * mm, "end": v(7.43, 58.69) * mm});
            skLineSegment(sketch, "E500", {"start": v(7.43, 58.69) * mm, "end": v(7.84, 58.41) * mm});
            skLineSegment(sketch, "E501", {"start": v(7.84, 58.41) * mm, "end": v(8.33, 58.25) * mm});
            skLineSegment(sketch, "E502", {"start": v(8.33, 58.25) * mm, "end": v(8.73, 58.21) * mm});
            skLineSegment(sketch, "E503", {"start": v(8.73, 58.21) * mm, "end": v(9.11, 58.25) * mm});
            skLineSegment(sketch, "E504", {"start": v(9.11, 58.25) * mm, "end": v(9.48, 58.37) * mm});
            skLineSegment(sketch, "E505", {"start": v(9.48, 58.37) * mm, "end": v(9.8, 58.55) * mm});
            skLineSegment(sketch, "E506", {"start": v(9.8, 58.55) * mm, "end": v(10.1, 58.8) * mm});
            skLineSegment(sketch, "E507", {"start": v(10.1, 58.8) * mm, "end": v(10.33, 59.1) * mm});
            skLineSegment(sketch, "E508", {"start": v(10.33, 59.1) * mm, "end": v(10.5, 59.44) * mm});
            skLineSegment(sketch, "E509", {"start": v(10.5, 59.44) * mm, "end": v(10.6, 59.83) * mm});
            skLineSegment(sketch, "E510", {"start": v(10.6, 59.83) * mm, "end": v(10.6, 60.4) * mm});
            skLineSegment(sketch, "E511", {"start": v(10.6, 60.4) * mm, "end": v(10.47, 60.9) * mm});
            skLineSegment(sketch, "E512", {"start": v(10.47, 60.9) * mm, "end": v(10.19, 61.35) * mm});
            skLineSegment(sketch, "E513", {"start": v(10.19, 61.35) * mm, "end": v(9.76, 61.73) * mm});
            skLineSegment(sketch, "E514", {"start": v(9.76, 61.73) * mm, "end": v(9.7, 61.77) * mm});
            skLineSegment(sketch, "E515", {"start": v(9.7, 61.77) * mm, "end": v(9.66, 61.85) * mm});
            skLineSegment(sketch, "E516", {"start": v(9.66, 61.85) * mm, "end": v(9.68, 61.94) * mm});
            skLineSegment(sketch, "E517", {"start": v(9.68, 61.94) * mm, "end": v(9.75, 62) * mm});
            skLineSegment(sketch, "E518", {"start": v(9.75, 62) * mm, "end": v(9.85, 61.98) * mm});
            skLineSegment(sketch, "E519", {"start": v(9.85, 61.98) * mm, "end": v(10.18, 61.74) * mm});
            skLineSegment(sketch, "E520", {"start": v(10.18, 61.74) * mm, "end": v(10.5, 61.36) * mm});
            skLineSegment(sketch, "E521", {"start": v(10.5, 61.36) * mm, "end": v(10.73, 60.94) * mm});
            skLineSegment(sketch, "E522", {"start": v(10.73, 60.94) * mm, "end": v(10.86, 60.48) * mm});
            skLineSegment(sketch, "E523", {"start": v(10.86, 60.48) * mm, "end": v(10.88, 59.99) * mm});
            skLineSegment(sketch, "E524", {"start": v(10.88, 59.99) * mm, "end": v(10.83, 59.62) * mm});
            skLineSegment(sketch, "E525", {"start": v(10.83, 59.62) * mm, "end": v(10.71, 59.28) * mm});
            skLineSegment(sketch, "E526", {"start": v(10.71, 59.28) * mm, "end": v(10.55, 58.96) * mm});
            skLineSegment(sketch, "E527", {"start": v(10.55, 58.96) * mm, "end": v(10.33, 58.68) * mm});
            skLineSegment(sketch, "E528", {"start": v(10.33, 58.68) * mm, "end": v(10.07, 58.43) * mm});
            skLineSegment(sketch, "E529", {"start": v(10.07, 58.43) * mm, "end": v(9.77, 58.23) * mm});
            skLineSegment(sketch, "E530", {"start": v(9.77, 58.23) * mm, "end": v(9.44, 58.08) * mm});
            skLineSegment(sketch, "E531", {"start": v(9.44, 58.08) * mm, "end": v(9.09, 57.98) * mm});
            skLineSegment(sketch, "E532", {"start": v(9.09, 57.98) * mm, "end": v(8.71, 57.95) * mm});
            skLineSegment(sketch, "E533", {"start": v(9.11, 60.18) * mm, "end": v(9.11, 59.2) * mm});
            skLineSegment(sketch, "E534", {"start": v(9.11, 59.2) * mm, "end": v(9.1, 59.04) * mm});
            skLineSegment(sketch, "E535", {"start": v(9.1, 59.04) * mm, "end": v(9.03, 58.93) * mm});
            skLineSegment(sketch, "E536", {"start": v(9.03, 58.93) * mm, "end": v(8.92, 58.87) * mm});
            skLineSegment(sketch, "E537", {"start": v(8.92, 58.87) * mm, "end": v(8.76, 58.85) * mm});
            skLineSegment(sketch, "E538", {"start": v(8.76, 58.85) * mm, "end": v(8.56, 58.86) * mm});
            skLineSegment(sketch, "E539", {"start": v(8.56, 58.86) * mm, "end": v(8.38, 58.94) * mm});
            skLineSegment(sketch, "E540", {"start": v(8.38, 58.94) * mm, "end": v(8.3, 59.12) * mm});
            skLineSegment(sketch, "E541", {"start": v(8.3, 59.12) * mm, "end": v(8.3, 59.25) * mm});
            skLineSegment(sketch, "E542", {"start": v(8.3, 59.25) * mm, "end": v(8.3, 61.08) * mm});
            skLineSegment(sketch, "E543", {"start": v(8.3, 61.08) * mm, "end": v(8.32, 61.28) * mm});
            skLineSegment(sketch, "E544", {"start": v(8.32, 61.28) * mm, "end": v(8.4, 61.42) * mm});
            skLineSegment(sketch, "E545", {"start": v(8.4, 61.42) * mm, "end": v(8.53, 61.5) * mm});
            skLineSegment(sketch, "E546", {"start": v(8.53, 61.5) * mm, "end": v(8.73, 61.51) * mm});
            skLineSegment(sketch, "E547", {"start": v(8.73, 61.51) * mm, "end": v(8.88, 61.5) * mm});
            skLineSegment(sketch, "E548", {"start": v(8.88, 61.5) * mm, "end": v(9.05, 61.4) * mm});
            skLineSegment(sketch, "E549", {"start": v(9.05, 61.4) * mm, "end": v(9.11, 61.2) * mm});
            skLineSegment(sketch, "E550", {"start": v(9.11, 61.2) * mm, "end": v(9.11, 60.18) * mm});
            skLineSegment(sketch, "E551", {"start": v(-20.63, 60.24) * mm, "end": v(-20.63, 61.47) * mm});
            skLineSegment(sketch, "E552", {"start": v(-20.63, 61.47) * mm, "end": v(-20.62, 61.53) * mm});
            skLineSegment(sketch, "E553", {"start": v(-20.62, 61.53) * mm, "end": v(-20.57, 61.54) * mm});
            skLineSegment(sketch, "E554", {"start": v(-20.57, 61.54) * mm, "end": v(-20.12, 61.54) * mm});
            skLineSegment(sketch, "E555", {"start": v(-20.12, 61.54) * mm, "end": v(-20.08, 61.53) * mm});
            skLineSegment(sketch, "E556", {"start": v(-20.08, 61.53) * mm, "end": v(-20.06, 61.49) * mm});
            skLineSegment(sketch, "E557", {"start": v(-20.06, 61.49) * mm, "end": v(-20.06, 58.97) * mm});
            skLineSegment(sketch, "E558", {"start": v(-20.06, 58.97) * mm, "end": v(-20.08, 58.93) * mm});
            skLineSegment(sketch, "E559", {"start": v(-20.08, 58.93) * mm, "end": v(-20.12, 58.92) * mm});
            skLineSegment(sketch, "E560", {"start": v(-20.12, 58.92) * mm, "end": v(-20.57, 58.92) * mm});
            skLineSegment(sketch, "E561", {"start": v(-20.57, 58.92) * mm, "end": v(-20.62, 58.93) * mm});
            skLineSegment(sketch, "E562", {"start": v(-20.62, 58.93) * mm, "end": v(-20.63, 58.99) * mm});
            skLineSegment(sketch, "E563", {"start": v(-20.63, 58.99) * mm, "end": v(-20.63, 60.24) * mm});
            skLineSegment(sketch, "E564", {"start": v(8.25, 62.63) * mm, "end": v(8.28, 62.82) * mm});
            skLineSegment(sketch, "E565", {"start": v(8.28, 62.82) * mm, "end": v(8.38, 62.97) * mm});
            skLineSegment(sketch, "E566", {"start": v(8.38, 62.97) * mm, "end": v(8.53, 63.07) * mm});
            skLineSegment(sketch, "E567", {"start": v(8.53, 63.07) * mm, "end": v(8.72, 63.11) * mm});
            skLineSegment(sketch, "E568", {"start": v(8.72, 63.11) * mm, "end": v(8.9, 63.07) * mm});
            skLineSegment(sketch, "E569", {"start": v(8.9, 63.07) * mm, "end": v(9.06, 62.97) * mm});
            skLineSegment(sketch, "E570", {"start": v(9.06, 62.97) * mm, "end": v(9.16, 62.82) * mm});
            skLineSegment(sketch, "E571", {"start": v(9.16, 62.82) * mm, "end": v(9.2, 62.64) * mm});
            skLineSegment(sketch, "E572", {"start": v(9.2, 62.64) * mm, "end": v(9.16, 62.45) * mm});
            skLineSegment(sketch, "E573", {"start": v(9.16, 62.45) * mm, "end": v(9.06, 62.3) * mm});
            skLineSegment(sketch, "E574", {"start": v(9.06, 62.3) * mm, "end": v(8.9, 62.2) * mm});
            skLineSegment(sketch, "E575", {"start": v(8.9, 62.2) * mm, "end": v(8.72, 62.16) * mm});
            skLineSegment(sketch, "E576", {"start": v(8.72, 62.16) * mm, "end": v(8.54, 62.2) * mm});
            skLineSegment(sketch, "E577", {"start": v(8.54, 62.2) * mm, "end": v(8.38, 62.3) * mm});
            skLineSegment(sketch, "E578", {"start": v(8.38, 62.3) * mm, "end": v(8.28, 62.45) * mm});
            skLineSegment(sketch, "E579", {"start": v(8.28, 62.45) * mm, "end": v(8.25, 62.63) * mm});
            skSolve(sketch);
        }
        {
            var Q0;
            Q0 = qSketchRegion(id + "F9", true);
            extrude(context, id + "F10", {"entities" : qUnion([Q0]), "endBound" : BoundingType.SYMMETRIC, "depth" : 2.4 * mm, "offsetDistance" : 25 * mm});
        }
        {
            var Q0;
            Q0=makeQuery(id+"F10.opExtrude","SWEPT_BODY",BODY,{"disambiguationData":[OSD([sQuery(id+"F9.wireOp",EDGE,"E261"),sQuery(id+"F9.wireOp",EDGE,"E262"),sQuery(id+"F9.wireOp",EDGE,"E263"),sQuery(id+"F9.wireOp",EDGE,"E264"),sQuery(id+"F9.wireOp",EDGE,"E265"),sQuery(id+"F9.wireOp",EDGE,"E266"),sQuery(id+"F9.wireOp",EDGE,"E267"),sQuery(id+"F9.wireOp",EDGE,"E268"),sQuery(id+"F9.wireOp",EDGE,"E269"),sQuery(id+"F9.wireOp",EDGE,"E270"),sQuery(id+"F9.wireOp",EDGE,"E271"),sQuery(id+"F9.wireOp",EDGE,"E272"),sQuery(id+"F9.wireOp",EDGE,"E273"),sQuery(id+"F9.wireOp",EDGE,"E274"),sQuery(id+"F9.wireOp",EDGE,"E275"),sQuery(id+"F9.wireOp",EDGE,"E276"),sQuery(id+"F9.wireOp",EDGE,"E277"),sQuery(id+"F9.wireOp",EDGE,"E278"),sQuery(id+"F9.wireOp",EDGE,"E279"),sQuery(id+"F9.wireOp",EDGE,"E280"),sQuery(id+"F9.wireOp",EDGE,"E281"),sQuery(id+"F9.wireOp",EDGE,"E282"),sQuery(id+"F9.wireOp",EDGE,"E283"),sQuery(id+"F9.wireOp",EDGE,"E284"),sQuery(id+"F9.wireOp",EDGE,"E285"),sQuery(id+"F9.wireOp",EDGE,"E286"),sQuery(id+"F9.wireOp",EDGE,"E287"),sQuery(id+"F9.wireOp",EDGE,"E288"),sQuery(id+"F9.wireOp",EDGE,"E289"),sQuery(id+"F9.wireOp",EDGE,"E290"),sQuery(id+"F9.wireOp",EDGE,"E291"),sQuery(id+"F9.wireOp",EDGE,"E292"),sQuery(id+"F9.wireOp",EDGE,"E293"),sQuery(id+"F9.wireOp",EDGE,"E294"),sQuery(id+"F9.wireOp",EDGE,"E295"),sQuery(id+"F9.wireOp",EDGE,"E296"),sQuery(id+"F9.wireOp",EDGE,"E297"),sQuery(id+"F9.wireOp",EDGE,"E298"),sQuery(id+"F9.wireOp",EDGE,"E299"),sQuery(id+"F9.wireOp",EDGE,"E300"),sQuery(id+"F9.wireOp",EDGE,"E301"),sQuery(id+"F9.wireOp",EDGE,"E302"),sQuery(id+"F9.wireOp",EDGE,"E303"),sQuery(id+"F9.wireOp",EDGE,"E304"),sQuery(id+"F9.wireOp",EDGE,"E305"),sQuery(id+"F9.wireOp",EDGE,"E306"),sQuery(id+"F9.wireOp",EDGE,"E307"),sQuery(id+"F9.wireOp",EDGE,"E308"),sQuery(id+"F9.wireOp",EDGE,"E309"),sQuery(id+"F9.wireOp",EDGE,"E310"),sQuery(id+"F9.wireOp",EDGE,"E311"),sQuery(id+"F9.wireOp",EDGE,"E312"),sQuery(id+"F9.wireOp",EDGE,"E313"),sQuery(id+"F9.wireOp",EDGE,"E314"),sQuery(id+"F9.wireOp",EDGE,"E315"),sQuery(id+"F9.wireOp",EDGE,"E316"),sQuery(id+"F9.wireOp",EDGE,"E317"),sQuery(id+"F9.wireOp",EDGE,"E318"),sQuery(id+"F9.wireOp",EDGE,"E319"),sQuery(id+"F9.wireOp",EDGE,"E320")])]});
            var Q1;
            Q1=makeQuery(id+"F10.opExtrude","SWEPT_BODY",BODY,{"disambiguationData":[OSD([sQuery(id+"F9.wireOp",EDGE,"E476"),sQuery(id+"F9.wireOp",EDGE,"E477"),sQuery(id+"F9.wireOp",EDGE,"E478"),sQuery(id+"F9.wireOp",EDGE,"E479"),sQuery(id+"F9.wireOp",EDGE,"E480"),sQuery(id+"F9.wireOp",EDGE,"E481"),sQuery(id+"F9.wireOp",EDGE,"E482"),sQuery(id+"F9.wireOp",EDGE,"E483"),sQuery(id+"F9.wireOp",EDGE,"E484"),sQuery(id+"F9.wireOp",EDGE,"E485"),sQuery(id+"F9.wireOp",EDGE,"E486"),sQuery(id+"F9.wireOp",EDGE,"E487"),sQuery(id+"F9.wireOp",EDGE,"E488"),sQuery(id+"F9.wireOp",EDGE,"E489"),sQuery(id+"F9.wireOp",EDGE,"E490"),sQuery(id+"F9.wireOp",EDGE,"E491"),sQuery(id+"F9.wireOp",EDGE,"E492"),sQuery(id+"F9.wireOp",EDGE,"E493"),sQuery(id+"F9.wireOp",EDGE,"E494"),sQuery(id+"F9.wireOp",EDGE,"E495"),sQuery(id+"F9.wireOp",EDGE,"E496"),sQuery(id+"F9.wireOp",EDGE,"E497"),sQuery(id+"F9.wireOp",EDGE,"E498"),sQuery(id+"F9.wireOp",EDGE,"E499"),sQuery(id+"F9.wireOp",EDGE,"E500"),sQuery(id+"F9.wireOp",EDGE,"E501"),sQuery(id+"F9.wireOp",EDGE,"E502"),sQuery(id+"F9.wireOp",EDGE,"E503"),sQuery(id+"F9.wireOp",EDGE,"E504"),sQuery(id+"F9.wireOp",EDGE,"E505"),sQuery(id+"F9.wireOp",EDGE,"E506"),sQuery(id+"F9.wireOp",EDGE,"E507"),sQuery(id+"F9.wireOp",EDGE,"E508"),sQuery(id+"F9.wireOp",EDGE,"E509"),sQuery(id+"F9.wireOp",EDGE,"E510"),sQuery(id+"F9.wireOp",EDGE,"E511"),sQuery(id+"F9.wireOp",EDGE,"E512"),sQuery(id+"F9.wireOp",EDGE,"E513"),sQuery(id+"F9.wireOp",EDGE,"E514"),sQuery(id+"F9.wireOp",EDGE,"E515"),sQuery(id+"F9.wireOp",EDGE,"E516"),sQuery(id+"F9.wireOp",EDGE,"E517"),sQuery(id+"F9.wireOp",EDGE,"E518"),sQuery(id+"F9.wireOp",EDGE,"E519"),sQuery(id+"F9.wireOp",EDGE,"E520"),sQuery(id+"F9.wireOp",EDGE,"E521"),sQuery(id+"F9.wireOp",EDGE,"E522"),sQuery(id+"F9.wireOp",EDGE,"E523"),sQuery(id+"F9.wireOp",EDGE,"E524"),sQuery(id+"F9.wireOp",EDGE,"E525"),sQuery(id+"F9.wireOp",EDGE,"E526"),sQuery(id+"F9.wireOp",EDGE,"E527"),sQuery(id+"F9.wireOp",EDGE,"E528"),sQuery(id+"F9.wireOp",EDGE,"E529"),sQuery(id+"F9.wireOp",EDGE,"E530"),sQuery(id+"F9.wireOp",EDGE,"E531"),sQuery(id+"F9.wireOp",EDGE,"E532")])]});
            var Q2;
            Q2=makeQuery(id+"F10.opExtrude","SWEPT_BODY",BODY,{"disambiguationData":[OSD([sQuery(id+"F9.wireOp",EDGE,"E533"),sQuery(id+"F9.wireOp",EDGE,"E534"),sQuery(id+"F9.wireOp",EDGE,"E535"),sQuery(id+"F9.wireOp",EDGE,"E536"),sQuery(id+"F9.wireOp",EDGE,"E537"),sQuery(id+"F9.wireOp",EDGE,"E538"),sQuery(id+"F9.wireOp",EDGE,"E539"),sQuery(id+"F9.wireOp",EDGE,"E540"),sQuery(id+"F9.wireOp",EDGE,"E541"),sQuery(id+"F9.wireOp",EDGE,"E542"),sQuery(id+"F9.wireOp",EDGE,"E543"),sQuery(id+"F9.wireOp",EDGE,"E544"),sQuery(id+"F9.wireOp",EDGE,"E545"),sQuery(id+"F9.wireOp",EDGE,"E546"),sQuery(id+"F9.wireOp",EDGE,"E547"),sQuery(id+"F9.wireOp",EDGE,"E548"),sQuery(id+"F9.wireOp",EDGE,"E549"),sQuery(id+"F9.wireOp",EDGE,"E550")])]});
            var Q3;
            Q3=makeQuery(id+"F10.opExtrude","SWEPT_BODY",BODY,{"disambiguationData":[OSD([sQuery(id+"F9.wireOp",EDGE,"E564"),sQuery(id+"F9.wireOp",EDGE,"E565"),sQuery(id+"F9.wireOp",EDGE,"E566"),sQuery(id+"F9.wireOp",EDGE,"E567"),sQuery(id+"F9.wireOp",EDGE,"E568"),sQuery(id+"F9.wireOp",EDGE,"E569"),sQuery(id+"F9.wireOp",EDGE,"E570"),sQuery(id+"F9.wireOp",EDGE,"E571"),sQuery(id+"F9.wireOp",EDGE,"E572"),sQuery(id+"F9.wireOp",EDGE,"E573"),sQuery(id+"F9.wireOp",EDGE,"E574"),sQuery(id+"F9.wireOp",EDGE,"E575"),sQuery(id+"F9.wireOp",EDGE,"E576"),sQuery(id+"F9.wireOp",EDGE,"E577"),sQuery(id+"F9.wireOp",EDGE,"E578"),sQuery(id+"F9.wireOp",EDGE,"E579")])]});
            var Q4;
            Q4=makeQuery(id+"F10.opExtrude","SWEPT_BODY",BODY,{"disambiguationData":[OSD([sQuery(id+"F9.wireOp",EDGE,"E22"),sQuery(id+"F9.wireOp",EDGE,"E23"),sQuery(id+"F9.wireOp",EDGE,"E24"),sQuery(id+"F9.wireOp",EDGE,"E25"),sQuery(id+"F9.wireOp",EDGE,"E26"),sQuery(id+"F9.wireOp",EDGE,"E27"),sQuery(id+"F9.wireOp",EDGE,"E28"),sQuery(id+"F9.wireOp",EDGE,"E29"),sQuery(id+"F9.wireOp",EDGE,"E30"),sQuery(id+"F9.wireOp",EDGE,"E31"),sQuery(id+"F9.wireOp",EDGE,"E32"),sQuery(id+"F9.wireOp",EDGE,"E33"),sQuery(id+"F9.wireOp",EDGE,"E34"),sQuery(id+"F9.wireOp",EDGE,"E35"),sQuery(id+"F9.wireOp",EDGE,"E36"),sQuery(id+"F9.wireOp",EDGE,"E37"),sQuery(id+"F9.wireOp",EDGE,"E38"),sQuery(id+"F9.wireOp",EDGE,"E39"),sQuery(id+"F9.wireOp",EDGE,"E40"),sQuery(id+"F9.wireOp",EDGE,"E41"),sQuery(id+"F9.wireOp",EDGE,"E42"),sQuery(id+"F9.wireOp",EDGE,"E43"),sQuery(id+"F9.wireOp",EDGE,"E44"),sQuery(id+"F9.wireOp",EDGE,"E45"),sQuery(id+"F9.wireOp",EDGE,"E46"),sQuery(id+"F9.wireOp",EDGE,"E47"),sQuery(id+"F9.wireOp",EDGE,"E48"),sQuery(id+"F9.wireOp",EDGE,"E49"),sQuery(id+"F9.wireOp",EDGE,"E50"),sQuery(id+"F9.wireOp",EDGE,"E51"),sQuery(id+"F9.wireOp",EDGE,"E52"),sQuery(id+"F9.wireOp",EDGE,"E53"),sQuery(id+"F9.wireOp",EDGE,"E54"),sQuery(id+"F9.wireOp",EDGE,"E55"),sQuery(id+"F9.wireOp",EDGE,"E56"),sQuery(id+"F9.wireOp",EDGE,"E57"),sQuery(id+"F9.wireOp",EDGE,"E58"),sQuery(id+"F9.wireOp",EDGE,"E59"),sQuery(id+"F9.wireOp",EDGE,"E60"),sQuery(id+"F9.wireOp",EDGE,"E61"),sQuery(id+"F9.wireOp",EDGE,"E62"),sQuery(id+"F9.wireOp",EDGE,"E63"),sQuery(id+"F9.wireOp",EDGE,"E64"),sQuery(id+"F9.wireOp",EDGE,"E65"),sQuery(id+"F9.wireOp",EDGE,"E66"),sQuery(id+"F9.wireOp",EDGE,"E67"),sQuery(id+"F9.wireOp",EDGE,"E68"),sQuery(id+"F9.wireOp",EDGE,"E69"),sQuery(id+"F9.wireOp",EDGE,"E70"),sQuery(id+"F9.wireOp",EDGE,"E71"),sQuery(id+"F9.wireOp",EDGE,"E72"),sQuery(id+"F9.wireOp",EDGE,"E73"),sQuery(id+"F9.wireOp",EDGE,"E74"),sQuery(id+"F9.wireOp",EDGE,"E75"),sQuery(id+"F9.wireOp",EDGE,"E76"),sQuery(id+"F9.wireOp",EDGE,"E77"),sQuery(id+"F9.wireOp",EDGE,"E78"),sQuery(id+"F9.wireOp",EDGE,"E79"),sQuery(id+"F9.wireOp",EDGE,"E80"),sQuery(id+"F9.wireOp",EDGE,"E81"),sQuery(id+"F9.wireOp",EDGE,"E82"),sQuery(id+"F9.wireOp",EDGE,"E83"),sQuery(id+"F9.wireOp",EDGE,"E84"),sQuery(id+"F9.wireOp",EDGE,"E85"),sQuery(id+"F9.wireOp",EDGE,"E86"),sQuery(id+"F9.wireOp",EDGE,"E87")])]});
            var Q5;
            Q5=makeQuery(id+"F10.opExtrude","SWEPT_BODY",BODY,{"disambiguationData":[OSD([sQuery(id+"F9.wireOp",EDGE,"E3"),sQuery(id+"F9.wireOp",EDGE,"E4"),sQuery(id+"F9.wireOp",EDGE,"E5"),sQuery(id+"F9.wireOp",EDGE,"E6"),sQuery(id+"F9.wireOp",EDGE,"E7"),sQuery(id+"F9.wireOp",EDGE,"E8"),sQuery(id+"F9.wireOp",EDGE,"E9"),sQuery(id+"F9.wireOp",EDGE,"E10"),sQuery(id+"F9.wireOp",EDGE,"E11"),sQuery(id+"F9.wireOp",EDGE,"E12"),sQuery(id+"F9.wireOp",EDGE,"E13"),sQuery(id+"F9.wireOp",EDGE,"E14"),sQuery(id+"F9.wireOp",EDGE,"E15"),sQuery(id+"F9.wireOp",EDGE,"E16"),sQuery(id+"F9.wireOp",EDGE,"E17"),sQuery(id+"F9.wireOp",EDGE,"E18"),sQuery(id+"F9.wireOp",EDGE,"E19"),sQuery(id+"F9.wireOp",EDGE,"E20"),sQuery(id+"F9.wireOp",EDGE,"E21")])]});
            var Q6;
            Q6=makeQuery(id+"F10.opExtrude","SWEPT_BODY",BODY,{"disambiguationData":[OSD([sQuery(id+"F9.wireOp",EDGE,"E88"),sQuery(id+"F9.wireOp",EDGE,"E89"),sQuery(id+"F9.wireOp",EDGE,"E90"),sQuery(id+"F9.wireOp",EDGE,"E91"),sQuery(id+"F9.wireOp",EDGE,"E92"),sQuery(id+"F9.wireOp",EDGE,"E93"),sQuery(id+"F9.wireOp",EDGE,"E94"),sQuery(id+"F9.wireOp",EDGE,"E95"),sQuery(id+"F9.wireOp",EDGE,"E96"),sQuery(id+"F9.wireOp",EDGE,"E97"),sQuery(id+"F9.wireOp",EDGE,"E98"),sQuery(id+"F9.wireOp",EDGE,"E99"),sQuery(id+"F9.wireOp",EDGE,"E100"),sQuery(id+"F9.wireOp",EDGE,"E101"),sQuery(id+"F9.wireOp",EDGE,"E102"),sQuery(id+"F9.wireOp",EDGE,"E103"),sQuery(id+"F9.wireOp",EDGE,"E104"),sQuery(id+"F9.wireOp",EDGE,"E105"),sQuery(id+"F9.wireOp",EDGE,"E106"),sQuery(id+"F9.wireOp",EDGE,"E107"),sQuery(id+"F9.wireOp",EDGE,"E108"),sQuery(id+"F9.wireOp",EDGE,"E109"),sQuery(id+"F9.wireOp",EDGE,"E110"),sQuery(id+"F9.wireOp",EDGE,"E111"),sQuery(id+"F9.wireOp",EDGE,"E112"),sQuery(id+"F9.wireOp",EDGE,"E113"),sQuery(id+"F9.wireOp",EDGE,"E114"),sQuery(id+"F9.wireOp",EDGE,"E115"),sQuery(id+"F9.wireOp",EDGE,"E116"),sQuery(id+"F9.wireOp",EDGE,"E117"),sQuery(id+"F9.wireOp",EDGE,"E118"),sQuery(id+"F9.wireOp",EDGE,"E119"),sQuery(id+"F9.wireOp",EDGE,"E120"),sQuery(id+"F9.wireOp",EDGE,"E121"),sQuery(id+"F9.wireOp",EDGE,"E122"),sQuery(id+"F9.wireOp",EDGE,"E123"),sQuery(id+"F9.wireOp",EDGE,"E124"),sQuery(id+"F9.wireOp",EDGE,"E125"),sQuery(id+"F9.wireOp",EDGE,"E126"),sQuery(id+"F9.wireOp",EDGE,"E127"),sQuery(id+"F9.wireOp",EDGE,"E128"),sQuery(id+"F9.wireOp",EDGE,"E129"),sQuery(id+"F9.wireOp",EDGE,"E130"),sQuery(id+"F9.wireOp",EDGE,"E131"),sQuery(id+"F9.wireOp",EDGE,"E132"),sQuery(id+"F9.wireOp",EDGE,"E133"),sQuery(id+"F9.wireOp",EDGE,"E134"),sQuery(id+"F9.wireOp",EDGE,"E135"),sQuery(id+"F9.wireOp",EDGE,"E136"),sQuery(id+"F9.wireOp",EDGE,"E137"),sQuery(id+"F9.wireOp",EDGE,"E138"),sQuery(id+"F9.wireOp",EDGE,"E139"),sQuery(id+"F9.wireOp",EDGE,"E140"),sQuery(id+"F9.wireOp",EDGE,"E141"),sQuery(id+"F9.wireOp",EDGE,"E142")])]});
            var Q7;
            Q7=makeQuery(id+"F10.opExtrude","SWEPT_BODY",BODY,{"disambiguationData":[OSD([sQuery(id+"F9.wireOp",EDGE,"E143"),sQuery(id+"F9.wireOp",EDGE,"E144"),sQuery(id+"F9.wireOp",EDGE,"E145"),sQuery(id+"F9.wireOp",EDGE,"E146"),sQuery(id+"F9.wireOp",EDGE,"E147"),sQuery(id+"F9.wireOp",EDGE,"E148"),sQuery(id+"F9.wireOp",EDGE,"E149"),sQuery(id+"F9.wireOp",EDGE,"E150"),sQuery(id+"F9.wireOp",EDGE,"E151"),sQuery(id+"F9.wireOp",EDGE,"E152"),sQuery(id+"F9.wireOp",EDGE,"E153"),sQuery(id+"F9.wireOp",EDGE,"E154"),sQuery(id+"F9.wireOp",EDGE,"E155"),sQuery(id+"F9.wireOp",EDGE,"E156"),sQuery(id+"F9.wireOp",EDGE,"E157"),sQuery(id+"F9.wireOp",EDGE,"E158"),sQuery(id+"F9.wireOp",EDGE,"E159"),sQuery(id+"F9.wireOp",EDGE,"E160"),sQuery(id+"F9.wireOp",EDGE,"E161"),sQuery(id+"F9.wireOp",EDGE,"E162"),sQuery(id+"F9.wireOp",EDGE,"E163"),sQuery(id+"F9.wireOp",EDGE,"E164"),sQuery(id+"F9.wireOp",EDGE,"E165"),sQuery(id+"F9.wireOp",EDGE,"E166"),sQuery(id+"F9.wireOp",EDGE,"E167"),sQuery(id+"F9.wireOp",EDGE,"E168"),sQuery(id+"F9.wireOp",EDGE,"E169"),sQuery(id+"F9.wireOp",EDGE,"E170"),sQuery(id+"F9.wireOp",EDGE,"E171"),sQuery(id+"F9.wireOp",EDGE,"E172"),sQuery(id+"F9.wireOp",EDGE,"E173"),sQuery(id+"F9.wireOp",EDGE,"E174"),sQuery(id+"F9.wireOp",EDGE,"E175"),sQuery(id+"F9.wireOp",EDGE,"E176"),sQuery(id+"F9.wireOp",EDGE,"E177"),sQuery(id+"F9.wireOp",EDGE,"E178"),sQuery(id+"F9.wireOp",EDGE,"E179"),sQuery(id+"F9.wireOp",EDGE,"E180"),sQuery(id+"F9.wireOp",EDGE,"E181"),sQuery(id+"F9.wireOp",EDGE,"E182"),sQuery(id+"F9.wireOp",EDGE,"E183"),sQuery(id+"F9.wireOp",EDGE,"E184"),sQuery(id+"F9.wireOp",EDGE,"E185"),sQuery(id+"F9.wireOp",EDGE,"E186"),sQuery(id+"F9.wireOp",EDGE,"E187"),sQuery(id+"F9.wireOp",EDGE,"E188"),sQuery(id+"F9.wireOp",EDGE,"E189"),sQuery(id+"F9.wireOp",EDGE,"E190"),sQuery(id+"F9.wireOp",EDGE,"E191"),sQuery(id+"F9.wireOp",EDGE,"E192"),sQuery(id+"F9.wireOp",EDGE,"E193"),sQuery(id+"F9.wireOp",EDGE,"E194"),sQuery(id+"F9.wireOp",EDGE,"E195"),sQuery(id+"F9.wireOp",EDGE,"E196"),sQuery(id+"F9.wireOp",EDGE,"E197"),sQuery(id+"F9.wireOp",EDGE,"E198")])]});
            var Q8;
            Q8=makeQuery(id+"F10.opExtrude","SWEPT_BODY",BODY,{"disambiguationData":[OSD([sQuery(id+"F9.wireOp",EDGE,"E199"),sQuery(id+"F9.wireOp",EDGE,"E200"),sQuery(id+"F9.wireOp",EDGE,"E201"),sQuery(id+"F9.wireOp",EDGE,"E202"),sQuery(id+"F9.wireOp",EDGE,"E203"),sQuery(id+"F9.wireOp",EDGE,"E204"),sQuery(id+"F9.wireOp",EDGE,"E205"),sQuery(id+"F9.wireOp",EDGE,"E206"),sQuery(id+"F9.wireOp",EDGE,"E207"),sQuery(id+"F9.wireOp",EDGE,"E208"),sQuery(id+"F9.wireOp",EDGE,"E209"),sQuery(id+"F9.wireOp",EDGE,"E210"),sQuery(id+"F9.wireOp",EDGE,"E211"),sQuery(id+"F9.wireOp",EDGE,"E212"),sQuery(id+"F9.wireOp",EDGE,"E213"),sQuery(id+"F9.wireOp",EDGE,"E214"),sQuery(id+"F9.wireOp",EDGE,"E215"),sQuery(id+"F9.wireOp",EDGE,"E216"),sQuery(id+"F9.wireOp",EDGE,"E217"),sQuery(id+"F9.wireOp",EDGE,"E218"),sQuery(id+"F9.wireOp",EDGE,"E219"),sQuery(id+"F9.wireOp",EDGE,"E220"),sQuery(id+"F9.wireOp",EDGE,"E221"),sQuery(id+"F9.wireOp",EDGE,"E222"),sQuery(id+"F9.wireOp",EDGE,"E223"),sQuery(id+"F9.wireOp",EDGE,"E224"),sQuery(id+"F9.wireOp",EDGE,"E225"),sQuery(id+"F9.wireOp",EDGE,"E226"),sQuery(id+"F9.wireOp",EDGE,"E227"),sQuery(id+"F9.wireOp",EDGE,"E228"),sQuery(id+"F9.wireOp",EDGE,"E229"),sQuery(id+"F9.wireOp",EDGE,"E230"),sQuery(id+"F9.wireOp",EDGE,"E231"),sQuery(id+"F9.wireOp",EDGE,"E232"),sQuery(id+"F9.wireOp",EDGE,"E233"),sQuery(id+"F9.wireOp",EDGE,"E234"),sQuery(id+"F9.wireOp",EDGE,"E235"),sQuery(id+"F9.wireOp",EDGE,"E236"),sQuery(id+"F9.wireOp",EDGE,"E237"),sQuery(id+"F9.wireOp",EDGE,"E238"),sQuery(id+"F9.wireOp",EDGE,"E239"),sQuery(id+"F9.wireOp",EDGE,"E240"),sQuery(id+"F9.wireOp",EDGE,"E241"),sQuery(id+"F9.wireOp",EDGE,"E242"),sQuery(id+"F9.wireOp",EDGE,"E243"),sQuery(id+"F9.wireOp",EDGE,"E244"),sQuery(id+"F9.wireOp",EDGE,"E245"),sQuery(id+"F9.wireOp",EDGE,"E246"),sQuery(id+"F9.wireOp",EDGE,"E247"),sQuery(id+"F9.wireOp",EDGE,"E248"),sQuery(id+"F9.wireOp",EDGE,"E249"),sQuery(id+"F9.wireOp",EDGE,"E250"),sQuery(id+"F9.wireOp",EDGE,"E251"),sQuery(id+"F9.wireOp",EDGE,"E252"),sQuery(id+"F9.wireOp",EDGE,"E253"),sQuery(id+"F9.wireOp",EDGE,"E254"),sQuery(id+"F9.wireOp",EDGE,"E255"),sQuery(id+"F9.wireOp",EDGE,"E256"),sQuery(id+"F9.wireOp",EDGE,"E257"),sQuery(id+"F9.wireOp",EDGE,"E258"),sQuery(id+"F9.wireOp",EDGE,"E259"),sQuery(id+"F9.wireOp",EDGE,"E260")])]});
            var Q9;
            Q9=makeQuery(id+"F10.opExtrude","SWEPT_BODY",BODY,{"disambiguationData":[OSD([sQuery(id+"F9.wireOp",EDGE,"E321"),sQuery(id+"F9.wireOp",EDGE,"E322"),sQuery(id+"F9.wireOp",EDGE,"E323"),sQuery(id+"F9.wireOp",EDGE,"E324"),sQuery(id+"F9.wireOp",EDGE,"E325"),sQuery(id+"F9.wireOp",EDGE,"E326"),sQuery(id+"F9.wireOp",EDGE,"E327"),sQuery(id+"F9.wireOp",EDGE,"E328"),sQuery(id+"F9.wireOp",EDGE,"E329"),sQuery(id+"F9.wireOp",EDGE,"E330"),sQuery(id+"F9.wireOp",EDGE,"E331"),sQuery(id+"F9.wireOp",EDGE,"E332"),sQuery(id+"F9.wireOp",EDGE,"E333"),sQuery(id+"F9.wireOp",EDGE,"E334"),sQuery(id+"F9.wireOp",EDGE,"E335"),sQuery(id+"F9.wireOp",EDGE,"E336"),sQuery(id+"F9.wireOp",EDGE,"E337"),sQuery(id+"F9.wireOp",EDGE,"E338"),sQuery(id+"F9.wireOp",EDGE,"E339"),sQuery(id+"F9.wireOp",EDGE,"E340"),sQuery(id+"F9.wireOp",EDGE,"E341"),sQuery(id+"F9.wireOp",EDGE,"E342"),sQuery(id+"F9.wireOp",EDGE,"E343"),sQuery(id+"F9.wireOp",EDGE,"E344"),sQuery(id+"F9.wireOp",EDGE,"E345"),sQuery(id+"F9.wireOp",EDGE,"E346"),sQuery(id+"F9.wireOp",EDGE,"E347"),sQuery(id+"F9.wireOp",EDGE,"E348"),sQuery(id+"F9.wireOp",EDGE,"E349"),sQuery(id+"F9.wireOp",EDGE,"E350"),sQuery(id+"F9.wireOp",EDGE,"E351"),sQuery(id+"F9.wireOp",EDGE,"E352"),sQuery(id+"F9.wireOp",EDGE,"E353"),sQuery(id+"F9.wireOp",EDGE,"E354"),sQuery(id+"F9.wireOp",EDGE,"E355"),sQuery(id+"F9.wireOp",EDGE,"E356"),sQuery(id+"F9.wireOp",EDGE,"E357"),sQuery(id+"F9.wireOp",EDGE,"E358"),sQuery(id+"F9.wireOp",EDGE,"E359"),sQuery(id+"F9.wireOp",EDGE,"E360"),sQuery(id+"F9.wireOp",EDGE,"E361"),sQuery(id+"F9.wireOp",EDGE,"E362"),sQuery(id+"F9.wireOp",EDGE,"E363"),sQuery(id+"F9.wireOp",EDGE,"E364"),sQuery(id+"F9.wireOp",EDGE,"E365"),sQuery(id+"F9.wireOp",EDGE,"E366"),sQuery(id+"F9.wireOp",EDGE,"E367"),sQuery(id+"F9.wireOp",EDGE,"E368"),sQuery(id+"F9.wireOp",EDGE,"E369"),sQuery(id+"F9.wireOp",EDGE,"E370"),sQuery(id+"F9.wireOp",EDGE,"E371"),sQuery(id+"F9.wireOp",EDGE,"E372"),sQuery(id+"F9.wireOp",EDGE,"E373"),sQuery(id+"F9.wireOp",EDGE,"E374"),sQuery(id+"F9.wireOp",EDGE,"E375")])]});
            var Q10;
            Q10=makeQuery(id+"F10.opExtrude","SWEPT_BODY",BODY,{"disambiguationData":[OSD([sQuery(id+"F9.wireOp",EDGE,"E376"),sQuery(id+"F9.wireOp",EDGE,"E377"),sQuery(id+"F9.wireOp",EDGE,"E378"),sQuery(id+"F9.wireOp",EDGE,"E379"),sQuery(id+"F9.wireOp",EDGE,"E380"),sQuery(id+"F9.wireOp",EDGE,"E381"),sQuery(id+"F9.wireOp",EDGE,"E382"),sQuery(id+"F9.wireOp",EDGE,"E383"),sQuery(id+"F9.wireOp",EDGE,"E384"),sQuery(id+"F9.wireOp",EDGE,"E385"),sQuery(id+"F9.wireOp",EDGE,"E386"),sQuery(id+"F9.wireOp",EDGE,"E387"),sQuery(id+"F9.wireOp",EDGE,"E388"),sQuery(id+"F9.wireOp",EDGE,"E389"),sQuery(id+"F9.wireOp",EDGE,"E390"),sQuery(id+"F9.wireOp",EDGE,"E391"),sQuery(id+"F9.wireOp",EDGE,"E392"),sQuery(id+"F9.wireOp",EDGE,"E393"),sQuery(id+"F9.wireOp",EDGE,"E394"),sQuery(id+"F9.wireOp",EDGE,"E395"),sQuery(id+"F9.wireOp",EDGE,"E396"),sQuery(id+"F9.wireOp",EDGE,"E397"),sQuery(id+"F9.wireOp",EDGE,"E398"),sQuery(id+"F9.wireOp",EDGE,"E399"),sQuery(id+"F9.wireOp",EDGE,"E400"),sQuery(id+"F9.wireOp",EDGE,"E401"),sQuery(id+"F9.wireOp",EDGE,"E402"),sQuery(id+"F9.wireOp",EDGE,"E403"),sQuery(id+"F9.wireOp",EDGE,"E404"),sQuery(id+"F9.wireOp",EDGE,"E405"),sQuery(id+"F9.wireOp",EDGE,"E406"),sQuery(id+"F9.wireOp",EDGE,"E407"),sQuery(id+"F9.wireOp",EDGE,"E408"),sQuery(id+"F9.wireOp",EDGE,"E409"),sQuery(id+"F9.wireOp",EDGE,"E410"),sQuery(id+"F9.wireOp",EDGE,"E411"),sQuery(id+"F9.wireOp",EDGE,"E412"),sQuery(id+"F9.wireOp",EDGE,"E413"),sQuery(id+"F9.wireOp",EDGE,"E414"),sQuery(id+"F9.wireOp",EDGE,"E415")])]});
            var Q11;
            Q11=makeQuery(id+"F10.opExtrude","SWEPT_BODY",BODY,{"disambiguationData":[OSD([sQuery(id+"F9.wireOp",EDGE,"E416"),sQuery(id+"F9.wireOp",EDGE,"E417"),sQuery(id+"F9.wireOp",EDGE,"E418"),sQuery(id+"F9.wireOp",EDGE,"E419"),sQuery(id+"F9.wireOp",EDGE,"E420"),sQuery(id+"F9.wireOp",EDGE,"E421"),sQuery(id+"F9.wireOp",EDGE,"E422"),sQuery(id+"F9.wireOp",EDGE,"E423"),sQuery(id+"F9.wireOp",EDGE,"E424"),sQuery(id+"F9.wireOp",EDGE,"E425"),sQuery(id+"F9.wireOp",EDGE,"E426"),sQuery(id+"F9.wireOp",EDGE,"E427"),sQuery(id+"F9.wireOp",EDGE,"E428"),sQuery(id+"F9.wireOp",EDGE,"E429"),sQuery(id+"F9.wireOp",EDGE,"E430"),sQuery(id+"F9.wireOp",EDGE,"E431"),sQuery(id+"F9.wireOp",EDGE,"E432"),sQuery(id+"F9.wireOp",EDGE,"E433"),sQuery(id+"F9.wireOp",EDGE,"E434"),sQuery(id+"F9.wireOp",EDGE,"E435"),sQuery(id+"F9.wireOp",EDGE,"E436"),sQuery(id+"F9.wireOp",EDGE,"E437"),sQuery(id+"F9.wireOp",EDGE,"E438"),sQuery(id+"F9.wireOp",EDGE,"E439"),sQuery(id+"F9.wireOp",EDGE,"E440"),sQuery(id+"F9.wireOp",EDGE,"E441"),sQuery(id+"F9.wireOp",EDGE,"E442"),sQuery(id+"F9.wireOp",EDGE,"E443"),sQuery(id+"F9.wireOp",EDGE,"E444"),sQuery(id+"F9.wireOp",EDGE,"E445"),sQuery(id+"F9.wireOp",EDGE,"E446"),sQuery(id+"F9.wireOp",EDGE,"E447"),sQuery(id+"F9.wireOp",EDGE,"E448"),sQuery(id+"F9.wireOp",EDGE,"E449"),sQuery(id+"F9.wireOp",EDGE,"E450"),sQuery(id+"F9.wireOp",EDGE,"E451"),sQuery(id+"F9.wireOp",EDGE,"E452")])]});
            var Q12;
            Q12=makeQuery(id+"F10.opExtrude","SWEPT_BODY",BODY,{"disambiguationData":[OSD([sQuery(id+"F9.wireOp",EDGE,"E453"),sQuery(id+"F9.wireOp",EDGE,"E454"),sQuery(id+"F9.wireOp",EDGE,"E455"),sQuery(id+"F9.wireOp",EDGE,"E456"),sQuery(id+"F9.wireOp",EDGE,"E457"),sQuery(id+"F9.wireOp",EDGE,"E458"),sQuery(id+"F9.wireOp",EDGE,"E459"),sQuery(id+"F9.wireOp",EDGE,"E460"),sQuery(id+"F9.wireOp",EDGE,"E461"),sQuery(id+"F9.wireOp",EDGE,"E462"),sQuery(id+"F9.wireOp",EDGE,"E463"),sQuery(id+"F9.wireOp",EDGE,"E464"),sQuery(id+"F9.wireOp",EDGE,"E465"),sQuery(id+"F9.wireOp",EDGE,"E466"),sQuery(id+"F9.wireOp",EDGE,"E467"),sQuery(id+"F9.wireOp",EDGE,"E468"),sQuery(id+"F9.wireOp",EDGE,"E469"),sQuery(id+"F9.wireOp",EDGE,"E470"),sQuery(id+"F9.wireOp",EDGE,"E471"),sQuery(id+"F9.wireOp",EDGE,"E472"),sQuery(id+"F9.wireOp",EDGE,"E473"),sQuery(id+"F9.wireOp",EDGE,"E474"),sQuery(id+"F9.wireOp",EDGE,"E475")])]});
            var Q13;
            Q13=makeQuery(id+"F10.opExtrude","SWEPT_BODY",BODY,{"disambiguationData":[OSD([sQuery(id+"F9.wireOp",EDGE,"E551"),sQuery(id+"F9.wireOp",EDGE,"E552"),sQuery(id+"F9.wireOp",EDGE,"E553"),sQuery(id+"F9.wireOp",EDGE,"E554"),sQuery(id+"F9.wireOp",EDGE,"E555"),sQuery(id+"F9.wireOp",EDGE,"E556"),sQuery(id+"F9.wireOp",EDGE,"E557"),sQuery(id+"F9.wireOp",EDGE,"E558"),sQuery(id+"F9.wireOp",EDGE,"E559"),sQuery(id+"F9.wireOp",EDGE,"E560"),sQuery(id+"F9.wireOp",EDGE,"E561"),sQuery(id+"F9.wireOp",EDGE,"E562"),sQuery(id+"F9.wireOp",EDGE,"E563")])]});
            var Q14;
            Q14=makeQuery(id+"F10.opExtrude","CAP_VERTEX",VERTEX,{"disambiguationData":[OSD([sQuery(id+"F9.wireOp",EDGE,"E406"),sQuery(id+"F9.wireOp",EDGE,"E407")])],"isStart":false});
            transform(context, id + "F11", {"entities" : qUnion([Q0, Q1, Q2, Q3, Q4, Q5, Q6, Q7, Q8, Q9, Q10, Q11, Q12, Q13]), "transformType" : TransformType.SCALE_UNIFORMLY, "scale" : 1, "scalePoint" : qUnion([Q14]), "makeCopy" : false});
        }
    });
